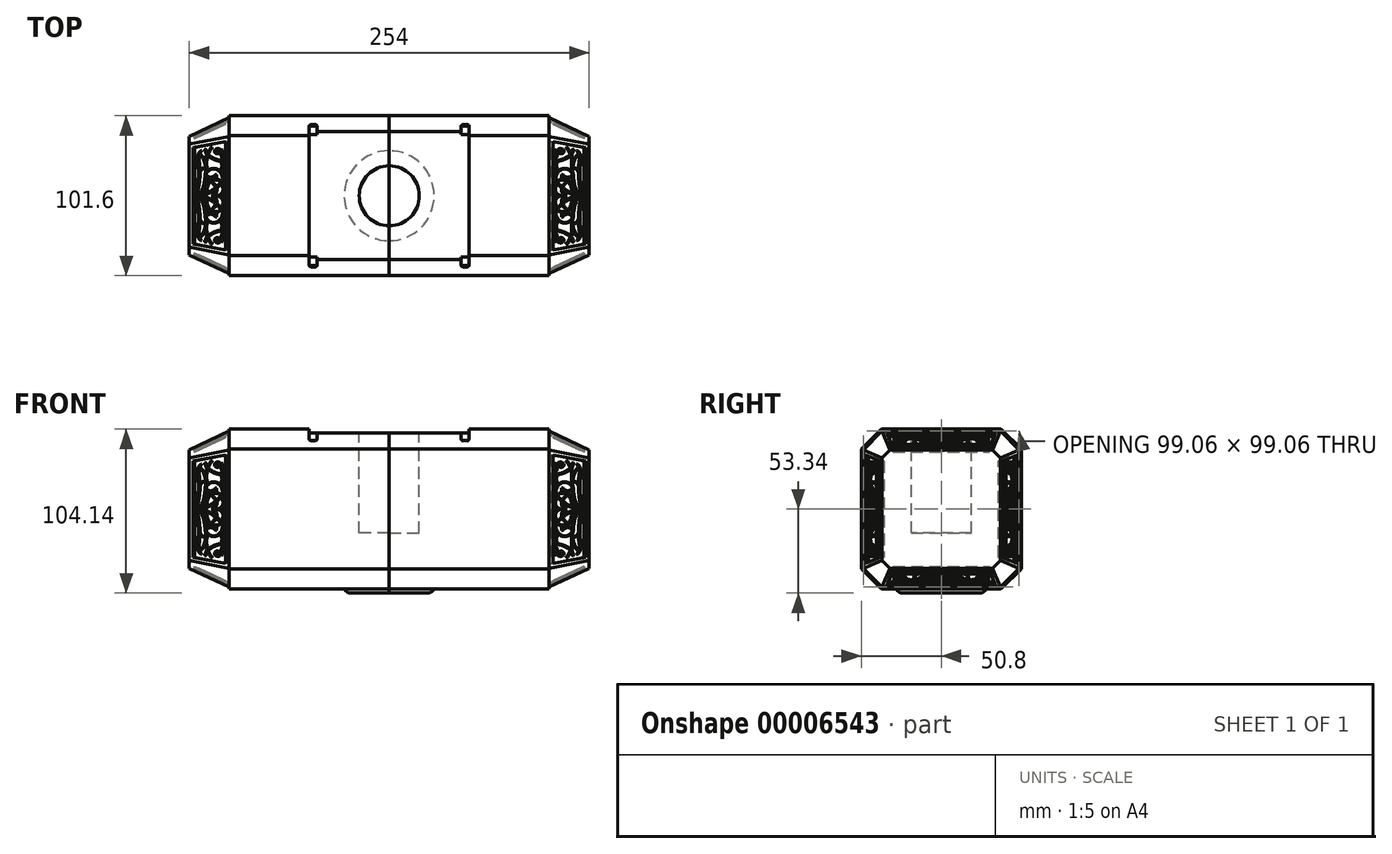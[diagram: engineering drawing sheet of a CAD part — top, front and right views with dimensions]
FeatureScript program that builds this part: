
annotation { "Feature Type Name" : "Feature", "Feature Type Description" : "" }
export const myFeature = defineFeature(function(context is Context, id is Id, definition is map)
    precondition{}
    {
        {
            var Q0;
            Q0=qCreatedBy(makeId("Top.planeOp"),FACE);
            var sketch = newSketch(context, id + "F0", { "sketchPlane" : qUnion([Q0])});
            skLineSegment(sketch, "E0.bottom", {"start": v(-101.6, -50.8) * mm, "end": v(0, -50.8) * mm});
            skLineSegment(sketch, "E0.top", {"start": v(-101.6, 50.8) * mm, "end": v(0, 50.8) * mm});
            skLineSegment(sketch, "E0.left", {"start": v(-101.6, -50.8) * mm, "end": v(-101.6, 50.8) * mm});
            skLineSegment(sketch, "E0.right", {"start": v(0, -50.8) * mm, "end": v(0, 50.8) * mm});
            skSolve(sketch);
        }
        {
            var Q0;
            Q0=makeQuery(id+"F0.imprint","IMPRINT",FACE,{"disambiguationData":[TD([[makeQuery(id+"F0.imprint","IMPRINT",EDGE,{"derivedFrom":sQuery(id+"F0.wireOp",EDGE,"E0.bottom")}),1.0]])]});
            extrude(context, id + "F1", {"entities" : qUnion([Q0]), "depth" : 101.6 * mm});
        }
        {
            var Q0;
            Q0=makeQuery(id+"F1.opExtrude","CAP_EDGE",EDGE,{"disambiguationData":[OSD([sQuery(id+"F0.wireOp",EDGE,"E0.bottom")])],"isStart":false});
            var Q1;
            Q1=makeQuery(id+"F1.opExtrude","CAP_EDGE",EDGE,{"disambiguationData":[OSD([sQuery(id+"F0.wireOp",EDGE,"E0.top")])],"isStart":false});
            var Q2;
            Q2=makeQuery(id+"F1.opExtrude","CAP_EDGE",EDGE,{"disambiguationData":[OSD([sQuery(id+"F0.wireOp",EDGE,"E0.bottom")])],"isStart":true});
            var Q3;
            Q3=makeQuery(id+"F1.opExtrude","CAP_EDGE",EDGE,{"disambiguationData":[OSD([sQuery(id+"F0.wireOp",EDGE,"E0.top")])],"isStart":true});
            chamfer(context, id + "F2", {"entities" : qUnion([Q0, Q1, Q2, Q3]), "width" : 12.7 * mm, "tangentPropagation" : true});
        }
        {
            var Q0;
            Q0=makeQuery(id+"F1.opExtrude","SWEPT_FACE",FACE,{"disambiguationData":[OSD([sQuery(id+"F0.wireOp",EDGE,"E0.left")])]});
            var sketch = newSketch(context, id + "F3", { "sketchPlane" : qUnion([Q0])});
            skLineSegment(sketch, "E1.0", {"start": v(-49.53, 88.37) * mm, "end": v(-37.57, 100.33) * mm});
            skLineSegment(sketch, "E1.1", {"start": v(37.57, 100.33) * mm, "end": v(-37.57, 100.33) * mm});
            skLineSegment(sketch, "E1.2", {"start": v(49.53, 88.37) * mm, "end": v(37.57, 100.33) * mm});
            skLineSegment(sketch, "E1.3", {"start": v(49.53, 88.37) * mm, "end": v(49.53, 13.23) * mm});
            skLineSegment(sketch, "E1.4", {"start": v(49.53, 13.23) * mm, "end": v(37.57, 1.27) * mm});
            skLineSegment(sketch, "E1.5", {"start": v(-49.53, 88.37) * mm, "end": v(-49.53, 13.23) * mm});
            skLineSegment(sketch, "E1.6", {"start": v(37.57, 1.27) * mm, "end": v(-37.57, 1.27) * mm});
            skLineSegment(sketch, "E1.7", {"start": v(-49.53, 13.23) * mm, "end": v(-37.57, 1.27) * mm});
            skSolve(sketch);
        }
        {
            var Q0;
            Q0 = qSketchRegion(id + "F3", true);
            extrude(context, id + "F4", {"entities" : qUnion([Q0]), "operationType" : NewBodyOperationType.ADD, "depth" : 25.4 * mm});
        }
        {
            var Q0;
            Q0=makeQuery(id+"F4.opExtrude","CAP_FACE",FACE,{"disambiguationData":[OSD([sQuery(id+"F3.wireOp",EDGE,"E1.0"),sQuery(id+"F3.wireOp",EDGE,"E1.1"),sQuery(id+"F3.wireOp",EDGE,"E1.2"),sQuery(id+"F3.wireOp",EDGE,"E1.3"),sQuery(id+"F3.wireOp",EDGE,"E1.4"),sQuery(id+"F3.wireOp",EDGE,"E1.5"),sQuery(id+"F3.wireOp",EDGE,"E1.6"),sQuery(id+"F3.wireOp",EDGE,"E1.7")])],"isStart":false});
            chamfer(context, id + "F5", {"entities" : qUnion([Q0]), "chamferType" : ChamferType.OFFSET_ANGLE, "width" : 25.4 * mm, "oppositeDirection" : false, "angle" : 25 * degree, "tangentPropagation" : true});
        }
        {
            var Q0;
            Q0=makeQuery(id+"F5.opChamfer","BLEND_FACE",FACE,{"disambiguationData":[OSD([sQuery(id+"F3.wireOp",EDGE,"E1.1")])]});
            var sketch = newSketch(context, id + "F6", { "sketchPlane" : qUnion([Q0])});
            skLineSegment(sketch, "E2.0", {"start": v(-75.17, -30.53) * mm, "end": v(-52.22, -34.55) * mm});
            skLineSegment(sketch, "E2.1", {"start": v(-75.17, -30.53) * mm, "end": v(-75.17, 30.53) * mm});
            skLineSegment(sketch, "E2.2", {"start": v(-52.22, 34.55) * mm, "end": v(-75.17, 30.53) * mm});
            skLineSegment(sketch, "E2.3", {"start": v(-52.22, -34.55) * mm, "end": v(-52.22, 34.55) * mm});
            skSolve(sketch);
        }
        {
            var Q0;
            Q0=makeQuery(id+"F6.imprint","IMPRINT",FACE,{"disambiguationData":[TD([[makeQuery(id+"F6.imprint","IMPRINT",EDGE,{"derivedFrom":sQuery(id+"F6.wireOp",EDGE,"E2.0")}),1.0]])]});
            extrude(context, id + "F7", {"entities" : qUnion([Q0]), "operationType" : NewBodyOperationType.REMOVE, "oppositeDirection" : true, "depth" : 2.54 * mm});
        }
        {
            var Q0;
            Q0=makeQuery(id+"F7.boolean.opBoolean","COPY",FACE,{"derivedFrom":makeQuery(id+"F7.opExtrude","CAP_FACE",FACE,{"disambiguationData":[OSD([sQuery(id+"F6.wireOp",EDGE,"E2.0"),sQuery(id+"F6.wireOp",EDGE,"E2.1"),sQuery(id+"F6.wireOp",EDGE,"E2.2"),sQuery(id+"F6.wireOp",EDGE,"E2.3")])],"isStart":false})});
            var sketch = newSketch(context, id + "F8", { "sketchPlane" : qUnion([Q0])});
            skLineSegment(sketch, "E3", {"start": v(-52.22, 34.55) * mm, "end": v(-52.22, -34.55) * mm});
            skLineSegment(sketch, "E4", {"start": v(-52.22, -34.55) * mm, "end": v(-75.17, -30.53) * mm, "construction": true});
            skLineSegment(sketch, "E5", {"start": v(-75.17, -30.53) * mm, "end": v(-75.17, 30.53) * mm});
            skLineSegment(sketch, "E6", {"start": v(-75.17, 30.53) * mm, "end": v(-52.22, 34.55) * mm, "construction": true});
            skLineSegment(sketch, "E7", {"start": v(-52.22, 0) * mm, "end": v(-75.17, 0) * mm, "construction": true});
            skArc(sketch, "E8", {"start": v(-55.35, -9.61) * mm, "mid": v(-55.7, -9.17) * mm, "end": v(-56.07, -8.74) * mm});
            skArc(sketch, "E9", {"start": v(-66.68, -14.4) * mm, "mid": v(-59.35, -16.72) * mm, "end": v(-55.08, -10.33) * mm});
            skArc(sketch, "E10", {"start": v(-59.94, -13.49) * mm, "mid": v(-63.02, -11.7) * mm, "end": v(-66.45, -12.68) * mm});
            skLineSegment(sketch, "E11", {"start": v(-59.94, -13.08) * mm, "end": v(-59.94, -10.38) * mm});
            skPoint(sketch, "E12.visualSharp", {"position": v(-55.12, -9.91) * mm});
            skArc(sketch, "E12.filletArc", {"start": v(-55.08, -10.33) * mm, "mid": v(-55.16, -9.95) * mm, "end": v(-55.35, -9.61) * mm});
            skPoint(sketch, "E13.visualSharp", {"position": v(-67.23, -13.49) * mm});
            skArc(sketch, "E13.filletArc", {"start": v(-66.45, -12.68) * mm, "mid": v(-66.9, -13.5) * mm, "end": v(-66.68, -14.4) * mm});
            skArc(sketch, "E14.0", {"start": v(-66.43, -15.12) * mm, "mid": v(-62.16, -17.3) * mm, "end": v(-57.53, -16.05) * mm});
            skArc(sketch, "E14.1", {"start": v(-66.61, -12.48) * mm, "mid": v(-66.77, -12.63) * mm, "end": v(-66.9, -12.8) * mm});
            skArc(sketch, "E14.2", {"start": v(-59.94, -13.08) * mm, "mid": v(-63.15, -11.43) * mm, "end": v(-66.61, -12.48) * mm});
            skLineSegment(sketch, "E15", {"start": v(-59.94, -13.49) * mm, "end": v(-59.6, -13.49) * mm});
            skLineSegment(sketch, "E16", {"start": v(-59.6, -10.38) * mm, "end": v(-59.6, -13.49) * mm});
            skArc(sketch, "E17", {"start": v(-59.6, -10.38) * mm, "mid": v(-57.65, -9.95) * mm, "end": v(-56.07, -8.74) * mm});
            skArc(sketch, "E18", {"start": v(-66.43, -1.56) * mm, "mid": v(-66.13, -6.4) * mm, "end": v(-62.66, -9.81) * mm});
            skArc(sketch, "E19.0", {"start": v(-59.6, -10.08) * mm, "mid": v(-57.78, -9.68) * mm, "end": v(-56.3, -8.54) * mm});
            skLineSegment(sketch, "E19.1", {"start": v(-59.94, -10.08) * mm, "end": v(-59.6, -10.08) * mm});
            skArc(sketch, "E19.2", {"start": v(-66.15, -1.65) * mm, "mid": v(-65.18, -7.43) * mm, "end": v(-59.94, -10.08) * mm});
            skArc(sketch, "E20", {"start": v(-67.23, -13.49) * mm, "mid": v(-68.26, -6.62) * mm, "end": v(-71.17, -0.32) * mm});
            skArc(sketch, "E21.trimOffspring", {"start": v(-66.9, -12.8) * mm, "mid": v(-67.19, -9.87) * mm, "end": v(-67.81, -7) * mm});
            skArc(sketch, "E22", {"start": v(-67.23, -13.49) * mm, "mid": v(-67.12, -14.04) * mm, "end": v(-66.89, -14.55) * mm});
            skArc(sketch, "E23.trimOffspring", {"start": v(-71.17, -0.32) * mm, "mid": v(-72.36, -0.16) * mm, "end": v(-73.55, -0.05) * mm});
            skArc(sketch, "E24.trimOffspring", {"start": v(-66.43, -1.56) * mm, "mid": v(-68.55, -0.88) * mm, "end": v(-70.73, -0.4) * mm});
            skArc(sketch, "E25", {"start": v(-56.3, -8.54) * mm, "mid": v(-57.92, -6.92) * mm, "end": v(-59.67, -5.43) * mm});
            skArc(sketch, "E26", {"start": v(-67.81, -7) * mm, "mid": v(-64.27, -9.61) * mm, "end": v(-59.94, -10.38) * mm});
            skArc(sketch, "E27", {"start": v(-68, -6.35) * mm, "mid": v(-65.6, -8.49) * mm, "end": v(-62.66, -9.81) * mm});
            skArc(sketch, "E28.trimOffspring", {"start": v(-68, -6.35) * mm, "mid": v(-69.17, -3.28) * mm, "end": v(-70.73, -0.4) * mm});
            skArc(sketch, "E29", {"start": v(-55.06, -9.54) * mm, "mid": v(-57.13, -7.05) * mm, "end": v(-59.52, -4.87) * mm});
            skArc(sketch, "E30", {"start": v(-54.83, -10.31) * mm, "mid": v(-54.92, -9.92) * mm, "end": v(-55.06, -9.54) * mm});
            skArc(sketch, "E31", {"start": v(-72.61, -22.4) * mm, "mid": v(-71.93, -11.1) * mm, "end": v(-74.2, -0.02) * mm});
            skArc(sketch, "E32", {"start": v(-72.61, -22.4) * mm, "mid": v(-72.38, -25.91) * mm, "end": v(-70.08, -28.6) * mm});
            skArc(sketch, "E33", {"start": v(-71.93, -22.54) * mm, "mid": v(-71.64, -25.76) * mm, "end": v(-70.08, -28.6) * mm});
            skArc(sketch, "E34", {"start": v(-71.93, -22.54) * mm, "mid": v(-71.5, -18.93) * mm, "end": v(-71.33, -15.3) * mm});
            skArc(sketch, "E35.trimOffspring", {"start": v(-74.2, -0.02) * mm, "mid": v(-74.68, 0) * mm, "end": v(-75.17, 0) * mm});
            skArc(sketch, "E36", {"start": v(-69.62, -24.91) * mm, "mid": v(-67.26, -20) * mm, "end": v(-66.89, -14.55) * mm});
            skArc(sketch, "E37", {"start": v(-69.6, -24.94) * mm, "mid": v(-68.07, -22.87) * mm, "end": v(-67, -20.54) * mm});
            skArc(sketch, "E38", {"start": v(-66.6, -19.05) * mm, "mid": v(-66.52, -22.38) * mm, "end": v(-65.74, -25.62) * mm});
            skArc(sketch, "E39", {"start": v(-67, -20.54) * mm, "mid": v(-66.8, -23.3) * mm, "end": v(-66.02, -25.97) * mm});
            skArc(sketch, "E40", {"start": v(-69.62, -24.91) * mm, "mid": v(-70.07, -25.46) * mm, "end": v(-69.6, -24.94) * mm});
            skArc(sketch, "E41", {"start": v(-63.4, -29.97) * mm, "mid": v(-62.9, -30.5) * mm, "end": v(-63.37, -29.95) * mm});
            skArc(sketch, "E42.trimOffspring", {"start": v(-66.6, -19.05) * mm, "mid": v(-66.36, -17.1) * mm, "end": v(-66.43, -15.12) * mm});
            skArc(sketch, "E43", {"start": v(-71.33, -14.67) * mm, "mid": v(-70.33, -16.2) * mm, "end": v(-68.84, -17.28) * mm});
            skArc(sketch, "E44", {"start": v(-71.33, -15.3) * mm, "mid": v(-70.26, -16.63) * mm, "end": v(-68.84, -17.59) * mm});
            skArc(sketch, "E45", {"start": v(-68.84, -17.59) * mm, "mid": v(-68.43, -17.43) * mm, "end": v(-68.84, -17.28) * mm});
            skArc(sketch, "E46.trimOffspring", {"start": v(-71.33, -14.67) * mm, "mid": v(-71.9, -7.28) * mm, "end": v(-73.55, -0.05) * mm});
            skArc(sketch, "E47", {"start": v(-56.91, -22) * mm, "mid": v(-55.44, -18.83) * mm, "end": v(-57.53, -16.05) * mm});
            skArc(sketch, "E48", {"start": v(-56.63, -22.43) * mm, "mid": v(-55.08, -18.89) * mm, "end": v(-56.8, -15.42) * mm});
            skArc(sketch, "E49", {"start": v(-56.91, -22) * mm, "mid": v(-60.9, -22.98) * mm, "end": v(-64.64, -24.68) * mm});
            skArc(sketch, "E50", {"start": v(-56.63, -22.43) * mm, "mid": v(-60.65, -23.45) * mm, "end": v(-64.33, -25.34) * mm});
            skArc(sketch, "E51", {"start": v(-64.64, -24.68) * mm, "mid": v(-65.22, -25.11) * mm, "end": v(-65.74, -25.62) * mm});
            skArc(sketch, "E52", {"start": v(-64.33, -25.34) * mm, "mid": v(-64.96, -25.72) * mm, "end": v(-65.51, -26.2) * mm});
            skArc(sketch, "E53", {"start": v(-67.08, -28.43) * mm, "mid": v(-67.42, -29.28) * mm, "end": v(-66.7, -28.71) * mm});
            skArc(sketch, "E54.trimOffspring", {"start": v(-65.51, -26.2) * mm, "mid": v(-64.57, -28.15) * mm, "end": v(-63.37, -29.95) * mm});
            skArc(sketch, "E55.trimOffspring", {"start": v(-66.02, -25.97) * mm, "mid": v(-66.7, -27.13) * mm, "end": v(-67.08, -28.43) * mm});
            skArc(sketch, "E56.trimOffspring", {"start": v(-65.78, -26.51) * mm, "mid": v(-64.73, -28.34) * mm, "end": v(-63.4, -29.97) * mm});
            skArc(sketch, "E57.trimOffspring", {"start": v(-65.78, -26.51) * mm, "mid": v(-66.4, -27.55) * mm, "end": v(-66.7, -28.71) * mm});
            skArc(sketch, "E58.trimOffspring", {"start": v(-56.8, -15.42) * mm, "mid": v(-56.04, -14.53) * mm, "end": v(-55.46, -13.53) * mm});
            skArc(sketch, "E59", {"start": v(-55.02, -24.61) * mm, "mid": v(-53.57, -18.63) * mm, "end": v(-55.12, -12.66) * mm});
            skArc(sketch, "E60", {"start": v(-55.02, -24.61) * mm, "mid": v(-55.54, -26.86) * mm, "end": v(-55.02, -29.1) * mm});
            skArc(sketch, "E61", {"start": v(-55.43, -24.24) * mm, "mid": v(-54.08, -18.88) * mm, "end": v(-55.46, -13.53) * mm});
            skArc(sketch, "E62", {"start": v(-55.43, -24.24) * mm, "mid": v(-55.84, -25.25) * mm, "end": v(-55.99, -26.33) * mm});
            skArc(sketch, "E63.trimOffspring", {"start": v(-55.12, -12.66) * mm, "mid": v(-54.87, -11.5) * mm, "end": v(-54.83, -10.31) * mm});
            skArc(sketch, "E64", {"start": v(-61.43, 0) * mm, "mid": v(-61.75, -1) * mm, "end": v(-61.34, -1.96) * mm});
            skArc(sketch, "E65", {"start": v(-61.69, 0) * mm, "mid": v(-62.06, -1.15) * mm, "end": v(-61.47, -2.21) * mm});
            skArc(sketch, "E66", {"start": v(-61.47, -2.21) * mm, "mid": v(-60.8, -2.33) * mm, "end": v(-60.15, -2.07) * mm});
            skArc(sketch, "E67", {"start": v(-61.34, -1.96) * mm, "mid": v(-60.78, -2.05) * mm, "end": v(-60.27, -1.82) * mm});
            skArc(sketch, "E68", {"start": v(-60.55, 0) * mm, "mid": v(-60.67, -0.95) * mm, "end": v(-60.27, -1.82) * mm});
            skArc(sketch, "E69", {"start": v(-60.18, 0) * mm, "mid": v(-60.26, -1.21) * mm, "end": v(-59.75, -2.32) * mm});
            skArc(sketch, "E70", {"start": v(-61.25, -7.6) * mm, "mid": v(-60.3, -6.64) * mm, "end": v(-59.67, -5.43) * mm});
            skArc(sketch, "E71", {"start": v(-61.48, -7.27) * mm, "mid": v(-60.56, -6.36) * mm, "end": v(-59.96, -5.2) * mm});
            skArc(sketch, "E72", {"start": v(-61.48, -7.27) * mm, "mid": v(-61.67, -7.64) * mm, "end": v(-61.25, -7.6) * mm});
            skArc(sketch, "E73.trimOffspring", {"start": v(-59.8, -4.64) * mm, "mid": v(-64.73, -1.7) * mm, "end": v(-70.2, 0) * mm});
            skArc(sketch, "E74.trimOffspring", {"start": v(-59.52, -4.87) * mm, "mid": v(-59.45, -3.57) * mm, "end": v(-59.75, -2.32) * mm});
            skArc(sketch, "E75.trimOffspring", {"start": v(-59.96, -5.2) * mm, "mid": v(-62.94, -3.23) * mm, "end": v(-66.15, -1.65) * mm});
            skArc(sketch, "E76.trimOffspring", {"start": v(-59.8, -4.64) * mm, "mid": v(-59.77, -3.33) * mm, "end": v(-60.15, -2.07) * mm});
            skArc(sketch, "E77", {"start": v(-59.98, -29.41) * mm, "mid": v(-57.3, -29.62) * mm, "end": v(-55.88, -27.35) * mm});
            skArc(sketch, "E78", {"start": v(-59.5, -28.83) * mm, "mid": v(-57.13, -28.43) * mm, "end": v(-55.99, -26.33) * mm});
            skArc(sketch, "E79", {"start": v(-57.78, -27.3) * mm, "mid": v(-59.28, -27.36) * mm, "end": v(-59.5, -28.83) * mm});
            skArc(sketch, "E80", {"start": v(-57.78, -27.3) * mm, "mid": v(-60.12, -27.07) * mm, "end": v(-59.98, -29.41) * mm});
            skArc(sketch, "E81.trimOffspring", {"start": v(-55.88, -27.35) * mm, "mid": v(-55.55, -28.28) * mm, "end": v(-55.02, -29.1) * mm});
            skArc(sketch, "E82", {"start": v(-54.19, -5.3) * mm, "mid": v(-54.2, -2.5) * mm, "end": v(-55.5, 0) * mm});
            skArc(sketch, "E83", {"start": v(-54.19, -5.3) * mm, "mid": v(-54.63, -7.58) * mm, "end": v(-53.98, -9.8) * mm});
            skArc(sketch, "E84", {"start": v(-55.16, -2.34) * mm, "mid": v(-57.14, -0.6) * mm, "end": v(-59.71, 0) * mm});
            skArc(sketch, "E85", {"start": v(-54.93, -5.38) * mm, "mid": v(-54.65, -3.83) * mm, "end": v(-55.16, -2.34) * mm});
            skArc(sketch, "E86", {"start": v(-54.93, -5.38) * mm, "mid": v(-55.04, -7.72) * mm, "end": v(-53.98, -9.8) * mm});
            skArc(sketch, "E87.0.MirrorCS", {"start": v(-55.08, 10.33) * mm, "mid": v(-55.16, 9.95) * mm, "end": v(-55.35, 9.61) * mm});
            skArc(sketch, "E87.1.MirrorCS", {"start": v(-66.61, 12.48) * mm, "mid": v(-66.77, 12.63) * mm, "end": v(-66.9, 12.8) * mm});
            skLineSegment(sketch, "E87.2.MirrorCS", {"start": v(-59.94, 13.49) * mm, "end": v(-59.6, 13.49) * mm});
            skArc(sketch, "E87.3.MirrorCS", {"start": v(-55.35, 9.61) * mm, "mid": v(-55.7, 9.17) * mm, "end": v(-56.07, 8.74) * mm});
            skPoint(sketch, "E87.4.MirrorP", {"position": v(-55.12, 9.91) * mm});
            skArc(sketch, "E87.5.MirrorCS", {"start": v(-68.84, 17.59) * mm, "mid": v(-68.43, 17.43) * mm, "end": v(-68.84, 17.28) * mm});
            skArc(sketch, "E87.6.MirrorCS", {"start": v(-55.43, 24.24) * mm, "mid": v(-54.08, 18.88) * mm, "end": v(-55.46, 13.53) * mm});
            skArc(sketch, "E87.7.MirrorCS", {"start": v(-55.06, 9.54) * mm, "mid": v(-57.13, 7.05) * mm, "end": v(-59.52, 4.87) * mm});
            skArc(sketch, "E87.8.MirrorCS", {"start": v(-59.98, 29.41) * mm, "mid": v(-57.3, 29.62) * mm, "end": v(-55.88, 27.35) * mm});
            skArc(sketch, "E87.9.MirrorCS", {"start": v(-60.18, 0) * mm, "mid": v(-60.26, 1.21) * mm, "end": v(-59.75, 2.32) * mm});
            skArc(sketch, "E87.10.MirrorCS", {"start": v(-67.08, 28.43) * mm, "mid": v(-67.42, 29.28) * mm, "end": v(-66.7, 28.71) * mm});
            skArc(sketch, "E87.11.MirrorCS", {"start": v(-69.6, 24.94) * mm, "mid": v(-68.07, 22.87) * mm, "end": v(-67, 20.54) * mm});
            skArc(sketch, "E87.12.MirrorCS", {"start": v(-66.9, 12.8) * mm, "mid": v(-67.19, 9.87) * mm, "end": v(-67.81, 7) * mm});
            skArc(sketch, "E87.13.MirrorCS", {"start": v(-54.93, 5.38) * mm, "mid": v(-54.65, 3.83) * mm, "end": v(-55.16, 2.34) * mm});
            skArc(sketch, "E87.14.MirrorCS", {"start": v(-68, 6.35) * mm, "mid": v(-65.6, 8.49) * mm, "end": v(-62.66, 9.81) * mm});
            skArc(sketch, "E87.15.MirrorCS", {"start": v(-71.33, 14.67) * mm, "mid": v(-70.33, 16.2) * mm, "end": v(-68.84, 17.28) * mm});
            skArc(sketch, "E87.16.MirrorCS", {"start": v(-55.02, 24.61) * mm, "mid": v(-53.57, 18.63) * mm, "end": v(-55.12, 12.66) * mm});
            skArc(sketch, "E87.17.MirrorCS", {"start": v(-59.96, 5.2) * mm, "mid": v(-62.94, 3.23) * mm, "end": v(-66.15, 1.65) * mm});
            skArc(sketch, "E87.18.MirrorCS", {"start": v(-55.43, 24.24) * mm, "mid": v(-55.84, 25.25) * mm, "end": v(-55.99, 26.33) * mm});
            skArc(sketch, "E87.19.MirrorCS", {"start": v(-71.33, 14.67) * mm, "mid": v(-71.9, 7.28) * mm, "end": v(-73.55, 0.05) * mm});
            skArc(sketch, "E87.20.MirrorCS", {"start": v(-54.83, 10.31) * mm, "mid": v(-54.92, 9.92) * mm, "end": v(-55.06, 9.54) * mm});
            skArc(sketch, "E87.21.MirrorCS", {"start": v(-59.5, 28.83) * mm, "mid": v(-57.13, 28.43) * mm, "end": v(-55.99, 26.33) * mm});
            skArc(sketch, "E87.22.MirrorCS", {"start": v(-55.16, 2.34) * mm, "mid": v(-57.14, 0.6) * mm, "end": v(-59.71, 0) * mm});
            skArc(sketch, "E87.23.MirrorCS", {"start": v(-64.33, 25.34) * mm, "mid": v(-64.96, 25.72) * mm, "end": v(-65.51, 26.2) * mm});
            skArc(sketch, "E87.24.MirrorCS", {"start": v(-60.55, 0) * mm, "mid": v(-60.67, 0.95) * mm, "end": v(-60.27, 1.82) * mm});
            skArc(sketch, "E87.25.MirrorCS", {"start": v(-67.23, 13.49) * mm, "mid": v(-68.26, 6.62) * mm, "end": v(-71.17, 0.32) * mm});
            skArc(sketch, "E87.26.MirrorCS", {"start": v(-69.62, 24.91) * mm, "mid": v(-67.26, 20) * mm, "end": v(-66.89, 14.55) * mm});
            skArc(sketch, "E87.27.MirrorCS", {"start": v(-67.23, 13.49) * mm, "mid": v(-67.12, 14.04) * mm, "end": v(-66.89, 14.55) * mm});
            skArc(sketch, "E87.28.MirrorCS", {"start": v(-66.6, 19.05) * mm, "mid": v(-66.52, 22.38) * mm, "end": v(-65.74, 25.62) * mm});
            skArc(sketch, "E87.29.MirrorCS", {"start": v(-65.51, 26.2) * mm, "mid": v(-64.57, 28.15) * mm, "end": v(-63.37, 29.95) * mm});
            skArc(sketch, "E87.30.MirrorCS", {"start": v(-66.45, 12.68) * mm, "mid": v(-66.9, 13.5) * mm, "end": v(-66.68, 14.4) * mm});
            skArc(sketch, "E87.31.MirrorCS", {"start": v(-54.19, 5.3) * mm, "mid": v(-54.2, 2.5) * mm, "end": v(-55.5, 0) * mm});
            skArc(sketch, "E87.32.MirrorCS", {"start": v(-61.25, 7.6) * mm, "mid": v(-60.3, 6.64) * mm, "end": v(-59.67, 5.43) * mm});
            skArc(sketch, "E87.33.MirrorCS", {"start": v(-54.93, 5.38) * mm, "mid": v(-55.04, 7.72) * mm, "end": v(-53.98, 9.8) * mm});
            skArc(sketch, "E87.34.MirrorCS", {"start": v(-66.43, 15.12) * mm, "mid": v(-62.16, 17.3) * mm, "end": v(-57.53, 16.05) * mm});
            skArc(sketch, "E87.35.MirrorCS", {"start": v(-61.47, 2.21) * mm, "mid": v(-60.8, 2.33) * mm, "end": v(-60.15, 2.07) * mm});
            skArc(sketch, "E87.36.MirrorCS", {"start": v(-56.63, 22.43) * mm, "mid": v(-60.65, 23.45) * mm, "end": v(-64.33, 25.34) * mm});
            skArc(sketch, "E87.37.MirrorCS", {"start": v(-71.93, 22.54) * mm, "mid": v(-71.5, 18.93) * mm, "end": v(-71.33, 15.3) * mm});
            skArc(sketch, "E87.38.MirrorCS", {"start": v(-55.12, 12.66) * mm, "mid": v(-54.87, 11.5) * mm, "end": v(-54.83, 10.31) * mm});
            skLineSegment(sketch, "E87.39.MirrorCS", {"start": v(-59.94, 10.08) * mm, "end": v(-59.6, 10.08) * mm});
            skArc(sketch, "E87.40.MirrorCS", {"start": v(-56.91, 22) * mm, "mid": v(-55.44, 18.83) * mm, "end": v(-57.53, 16.05) * mm});
            skArc(sketch, "E87.41.MirrorCS", {"start": v(-59.6, 10.38) * mm, "mid": v(-57.65, 9.95) * mm, "end": v(-56.07, 8.74) * mm});
            skArc(sketch, "E87.42.MirrorCS", {"start": v(-72.61, 22.4) * mm, "mid": v(-71.93, 11.1) * mm, "end": v(-74.2, 0.02) * mm});
            skArc(sketch, "E87.43.MirrorCS", {"start": v(-57.78, 27.3) * mm, "mid": v(-59.28, 27.36) * mm, "end": v(-59.5, 28.83) * mm});
            skLineSegment(sketch, "E87.44.MirrorCS", {"start": v(-59.6, 10.38) * mm, "end": v(-59.6, 13.49) * mm});
            skArc(sketch, "E87.45.MirrorCS", {"start": v(-56.3, 8.54) * mm, "mid": v(-57.92, 6.92) * mm, "end": v(-59.67, 5.43) * mm});
            skArc(sketch, "E87.46.MirrorCS", {"start": v(-59.8, 4.64) * mm, "mid": v(-64.73, 1.7) * mm, "end": v(-70.2, 0) * mm});
            skArc(sketch, "E87.47.MirrorCS", {"start": v(-63.4, 29.97) * mm, "mid": v(-62.9, 30.5) * mm, "end": v(-63.37, 29.95) * mm});
            skArc(sketch, "E87.48.MirrorCS", {"start": v(-65.78, 26.51) * mm, "mid": v(-66.4, 27.55) * mm, "end": v(-66.7, 28.71) * mm});
            skArc(sketch, "E87.49.MirrorCS", {"start": v(-59.94, 13.08) * mm, "mid": v(-63.15, 11.43) * mm, "end": v(-66.61, 12.48) * mm});
            skArc(sketch, "E87.50.MirrorCS", {"start": v(-66.43, 1.56) * mm, "mid": v(-68.55, 0.88) * mm, "end": v(-70.73, 0.4) * mm});
            skArc(sketch, "E87.51.MirrorCS", {"start": v(-66.68, 14.4) * mm, "mid": v(-59.35, 16.72) * mm, "end": v(-55.08, 10.33) * mm});
            skPoint(sketch, "E87.52.MirrorP", {"position": v(-67.23, 13.49) * mm});
            skArc(sketch, "E87.53.MirrorCS", {"start": v(-59.94, 13.49) * mm, "mid": v(-63.02, 11.7) * mm, "end": v(-66.45, 12.68) * mm});
            skLineSegment(sketch, "E87.54.MirrorCS", {"start": v(-59.94, 13.08) * mm, "end": v(-59.94, 10.38) * mm});
            skArc(sketch, "E87.55.MirrorCS", {"start": v(-69.62, 24.91) * mm, "mid": v(-70.07, 25.46) * mm, "end": v(-69.6, 24.94) * mm});
            skArc(sketch, "E87.56.MirrorCS", {"start": v(-71.33, 15.3) * mm, "mid": v(-70.26, 16.63) * mm, "end": v(-68.84, 17.59) * mm});
            skArc(sketch, "E87.57.MirrorCS", {"start": v(-68, 6.35) * mm, "mid": v(-69.17, 3.28) * mm, "end": v(-70.73, 0.4) * mm});
            skArc(sketch, "E87.58.MirrorCS", {"start": v(-59.8, 4.64) * mm, "mid": v(-59.77, 3.33) * mm, "end": v(-60.15, 2.07) * mm});
            skArc(sketch, "E87.59.MirrorCS", {"start": v(-61.69, 0) * mm, "mid": v(-62.06, 1.15) * mm, "end": v(-61.47, 2.21) * mm});
            skArc(sketch, "E87.60.MirrorCS", {"start": v(-56.91, 22) * mm, "mid": v(-60.9, 22.98) * mm, "end": v(-64.64, 24.68) * mm});
            skArc(sketch, "E87.61.MirrorCS", {"start": v(-59.6, 10.08) * mm, "mid": v(-57.78, 9.68) * mm, "end": v(-56.3, 8.54) * mm});
            skArc(sketch, "E87.62.MirrorCS", {"start": v(-55.02, 24.61) * mm, "mid": v(-55.54, 26.86) * mm, "end": v(-55.02, 29.1) * mm});
            skArc(sketch, "E87.63.MirrorCS", {"start": v(-71.93, 22.54) * mm, "mid": v(-71.64, 25.76) * mm, "end": v(-70.08, 28.6) * mm});
            skArc(sketch, "E87.64.MirrorCS", {"start": v(-54.19, 5.3) * mm, "mid": v(-54.63, 7.58) * mm, "end": v(-53.98, 9.8) * mm});
            skArc(sketch, "E87.65.MirrorCS", {"start": v(-61.34, 1.96) * mm, "mid": v(-60.78, 2.05) * mm, "end": v(-60.27, 1.82) * mm});
            skArc(sketch, "E87.66.MirrorCS", {"start": v(-74.2, 0.02) * mm, "mid": v(-74.68, 0) * mm, "end": v(-75.17, 0) * mm});
            skArc(sketch, "E87.67.MirrorCS", {"start": v(-66.15, 1.65) * mm, "mid": v(-65.18, 7.43) * mm, "end": v(-59.94, 10.08) * mm});
            skArc(sketch, "E87.68.MirrorCS", {"start": v(-67, 20.54) * mm, "mid": v(-66.8, 23.3) * mm, "end": v(-66.02, 25.97) * mm});
            skArc(sketch, "E87.69.MirrorCS", {"start": v(-56.63, 22.43) * mm, "mid": v(-55.08, 18.89) * mm, "end": v(-56.8, 15.42) * mm});
            skArc(sketch, "E87.70.MirrorCS", {"start": v(-71.17, 0.32) * mm, "mid": v(-72.36, 0.16) * mm, "end": v(-73.55, 0.05) * mm});
            skArc(sketch, "E87.71.MirrorCS", {"start": v(-55.88, 27.35) * mm, "mid": v(-55.55, 28.28) * mm, "end": v(-55.02, 29.1) * mm});
            skArc(sketch, "E87.72.MirrorCS", {"start": v(-61.43, 0) * mm, "mid": v(-61.75, 1) * mm, "end": v(-61.34, 1.96) * mm});
            skArc(sketch, "E87.73.MirrorCS", {"start": v(-59.52, 4.87) * mm, "mid": v(-59.45, 3.57) * mm, "end": v(-59.75, 2.32) * mm});
            skArc(sketch, "E87.74.MirrorCS", {"start": v(-64.64, 24.68) * mm, "mid": v(-65.22, 25.11) * mm, "end": v(-65.74, 25.62) * mm});
            skArc(sketch, "E87.75.MirrorCS", {"start": v(-66.02, 25.97) * mm, "mid": v(-66.7, 27.13) * mm, "end": v(-67.08, 28.43) * mm});
            skArc(sketch, "E87.76.MirrorCS", {"start": v(-61.48, 7.27) * mm, "mid": v(-60.56, 6.36) * mm, "end": v(-59.96, 5.2) * mm});
            skArc(sketch, "E87.77.MirrorCS", {"start": v(-67.81, 7) * mm, "mid": v(-64.27, 9.61) * mm, "end": v(-59.94, 10.38) * mm});
            skArc(sketch, "E87.78.MirrorCS", {"start": v(-66.6, 19.05) * mm, "mid": v(-66.36, 17.1) * mm, "end": v(-66.43, 15.12) * mm});
            skArc(sketch, "E87.79.MirrorCS", {"start": v(-57.78, 27.3) * mm, "mid": v(-60.12, 27.07) * mm, "end": v(-59.98, 29.41) * mm});
            skArc(sketch, "E87.80.MirrorCS", {"start": v(-61.48, 7.27) * mm, "mid": v(-61.67, 7.64) * mm, "end": v(-61.25, 7.6) * mm});
            skArc(sketch, "E87.81.MirrorCS", {"start": v(-72.61, 22.4) * mm, "mid": v(-72.38, 25.91) * mm, "end": v(-70.08, 28.6) * mm});
            skArc(sketch, "E87.82.MirrorCS", {"start": v(-65.78, 26.51) * mm, "mid": v(-64.73, 28.34) * mm, "end": v(-63.4, 29.97) * mm});
            skArc(sketch, "E87.83.MirrorCS", {"start": v(-56.8, 15.42) * mm, "mid": v(-56.04, 14.53) * mm, "end": v(-55.46, 13.53) * mm});
            skArc(sketch, "E87.84.MirrorCS", {"start": v(-66.43, 1.56) * mm, "mid": v(-66.13, 6.4) * mm, "end": v(-62.66, 9.81) * mm});
            skSolve(sketch);
        }
        {
            var Q0;
            Q0=makeQuery(id+"F8.imprint","IMPRINT",FACE,{"disambiguationData":[TD([[makeQuery(id+"F8.imprint","IMPRINT",EDGE,{"derivedFrom":sQuery(id+"F8.wireOp",EDGE,"E8")}),-1.0]])]});
            var Q1;
            Q1=makeQuery(id+"F8.imprint","IMPRINT",FACE,{"disambiguationData":[TD([[makeQuery(id+"F8.imprint","IMPRINT",EDGE,{"derivedFrom":sQuery(id+"F8.wireOp",EDGE,"E82")}),1.0]])]});
            extrude(context, id + "F9", {"entities" : qUnion([Q0, Q1]), "depth" : 1.27 * mm});
        }
        {
            var Q0;
            Q0=qCreatedBy(makeId("Front.planeOp"),FACE);
            var sketch = newSketch(context, id + "F10", { "sketchPlane" : qUnion([Q0])});
            skLineSegment(sketch, "E88", {"start": v(0, 50.8) * mm, "end": v(68.96, 50.8) * mm});
            skSolve(sketch);
        }
        {
            var Q0;
            Q0=makeQuery(id+"F5.opChamfer","BLEND_FACE",FACE,{"disambiguationData":[OSD([sQuery(id+"F3.wireOp",EDGE,"E1.5")])]});
            var sketch = newSketch(context, id + "F11", { "sketchPlane" : qUnion([Q0])});
            skLineSegment(sketch, "E89.0", {"start": v(96.63, 81.33) * mm, "end": v(73.69, 85.35) * mm});
            skLineSegment(sketch, "E89.1", {"start": v(96.63, 20.27) * mm, "end": v(96.63, 81.33) * mm});
            skLineSegment(sketch, "E89.2", {"start": v(96.63, 20.27) * mm, "end": v(73.69, 16.25) * mm});
            skLineSegment(sketch, "E89.3", {"start": v(73.69, 85.35) * mm, "end": v(73.69, 16.25) * mm});
            skSolve(sketch);
        }
        {
            var Q0;
            Q0=makeQuery(id+"F11.imprint","IMPRINT",FACE,{"disambiguationData":[TD([[makeQuery(id+"F11.imprint","IMPRINT",EDGE,{"derivedFrom":sQuery(id+"F11.wireOp",EDGE,"E89.0")}),1.0]])]});
            extrude(context, id + "F12", {"entities" : qUnion([Q0]), "operationType" : NewBodyOperationType.REMOVE, "oppositeDirection" : true, "depth" : 2.54 * mm});
        }
        {
            var Q0;
            Q0=makeQuery(id+"F5.opChamfer","BLEND_FACE",FACE,{"disambiguationData":[OSD([sQuery(id+"F3.wireOp",EDGE,"E1.6")])]});
            var sketch = newSketch(context, id + "F13", { "sketchPlane" : qUnion([Q0])});
            skLineSegment(sketch, "E90.0", {"start": v(-95.16, 34.55) * mm, "end": v(-118.1, 30.53) * mm});
            skLineSegment(sketch, "E90.1", {"start": v(-95.16, -34.55) * mm, "end": v(-95.16, 34.55) * mm});
            skLineSegment(sketch, "E90.2", {"start": v(-118.1, -30.53) * mm, "end": v(-95.16, -34.55) * mm});
            skLineSegment(sketch, "E90.3", {"start": v(-118.1, 30.53) * mm, "end": v(-118.1, -30.53) * mm});
            skSolve(sketch);
        }
        {
            var Q0;
            Q0=makeQuery(id+"F13.imprint","IMPRINT",FACE,{"disambiguationData":[TD([[makeQuery(id+"F13.imprint","IMPRINT",EDGE,{"derivedFrom":sQuery(id+"F13.wireOp",EDGE,"E90.0")}),1.0]])]});
            extrude(context, id + "F14", {"entities" : qUnion([Q0]), "operationType" : NewBodyOperationType.REMOVE, "oppositeDirection" : true, "depth" : 2.54 * mm});
        }
        {
            var Q0;
            Q0=makeQuery(id+"F5.opChamfer","BLEND_FACE",FACE,{"disambiguationData":[OSD([sQuery(id+"F3.wireOp",EDGE,"E1.3")])]});
            var sketch = newSketch(context, id + "F15", { "sketchPlane" : qUnion([Q0])});
            skLineSegment(sketch, "E91.0", {"start": v(-73.69, 85.35) * mm, "end": v(-96.63, 81.33) * mm});
            skLineSegment(sketch, "E91.1", {"start": v(-73.69, 16.25) * mm, "end": v(-73.69, 85.35) * mm});
            skLineSegment(sketch, "E91.2", {"start": v(-73.69, 16.25) * mm, "end": v(-96.63, 20.27) * mm});
            skLineSegment(sketch, "E91.3", {"start": v(-96.63, 81.33) * mm, "end": v(-96.63, 20.27) * mm});
            skSolve(sketch);
        }
        {
            var Q0;
            Q0=makeQuery(id+"F15.imprint","IMPRINT",FACE,{"disambiguationData":[TD([[makeQuery(id+"F15.imprint","IMPRINT",EDGE,{"derivedFrom":sQuery(id+"F15.wireOp",EDGE,"E91.0")}),1.0]])]});
            extrude(context, id + "F16", {"entities" : qUnion([Q0]), "operationType" : NewBodyOperationType.REMOVE, "oppositeDirection" : true, "depth" : 2.54 * mm});
        }
        {
            var Q0;
            Q0=makeQuery(id+"F9.opExtrude","SWEPT_BODY",BODY,{"disambiguationData":[OSD([sQuery(id+"F8.wireOp",EDGE,"E8"),sQuery(id+"F8.wireOp",EDGE,"E9"),sQuery(id+"F8.wireOp",EDGE,"E10"),sQuery(id+"F8.wireOp",EDGE,"E11"),sQuery(id+"F8.wireOp",EDGE,"E12.filletArc"),sQuery(id+"F8.wireOp",EDGE,"E13.filletArc"),sQuery(id+"F8.wireOp",EDGE,"E14.0"),sQuery(id+"F8.wireOp",EDGE,"E14.1"),sQuery(id+"F8.wireOp",EDGE,"E14.2"),sQuery(id+"F8.wireOp",EDGE,"E15"),sQuery(id+"F8.wireOp",EDGE,"E16"),sQuery(id+"F8.wireOp",EDGE,"E17"),sQuery(id+"F8.wireOp",EDGE,"E18"),sQuery(id+"F8.wireOp",EDGE,"E19.0"),sQuery(id+"F8.wireOp",EDGE,"E19.1"),sQuery(id+"F8.wireOp",EDGE,"E19.2"),sQuery(id+"F8.wireOp",EDGE,"E20"),sQuery(id+"F8.wireOp",EDGE,"E21.trimOffspring"),sQuery(id+"F8.wireOp",EDGE,"E22"),sQuery(id+"F8.wireOp",EDGE,"E23.trimOffspring"),sQuery(id+"F8.wireOp",EDGE,"E24.trimOffspring"),sQuery(id+"F8.wireOp",EDGE,"E25"),sQuery(id+"F8.wireOp",EDGE,"E26"),sQuery(id+"F8.wireOp",EDGE,"E27"),sQuery(id+"F8.wireOp",EDGE,"E28.trimOffspring"),sQuery(id+"F8.wireOp",EDGE,"E29"),sQuery(id+"F8.wireOp",EDGE,"E30"),sQuery(id+"F8.wireOp",EDGE,"E31"),sQuery(id+"F8.wireOp",EDGE,"E32"),sQuery(id+"F8.wireOp",EDGE,"E33"),sQuery(id+"F8.wireOp",EDGE,"E34"),sQuery(id+"F8.wireOp",EDGE,"E35.trimOffspring"),sQuery(id+"F8.wireOp",EDGE,"E36"),sQuery(id+"F8.wireOp",EDGE,"E37"),sQuery(id+"F8.wireOp",EDGE,"E38"),sQuery(id+"F8.wireOp",EDGE,"E39"),sQuery(id+"F8.wireOp",EDGE,"E40"),sQuery(id+"F8.wireOp",EDGE,"E41"),sQuery(id+"F8.wireOp",EDGE,"E42.trimOffspring"),sQuery(id+"F8.wireOp",EDGE,"E43"),sQuery(id+"F8.wireOp",EDGE,"E44"),sQuery(id+"F8.wireOp",EDGE,"E45"),sQuery(id+"F8.wireOp",EDGE,"E46.trimOffspring"),sQuery(id+"F8.wireOp",EDGE,"E47"),sQuery(id+"F8.wireOp",EDGE,"E48"),sQuery(id+"F8.wireOp",EDGE,"E49"),sQuery(id+"F8.wireOp",EDGE,"E50"),sQuery(id+"F8.wireOp",EDGE,"E51"),sQuery(id+"F8.wireOp",EDGE,"E52"),sQuery(id+"F8.wireOp",EDGE,"E53"),sQuery(id+"F8.wireOp",EDGE,"E54.trimOffspring"),sQuery(id+"F8.wireOp",EDGE,"E55.trimOffspring"),sQuery(id+"F8.wireOp",EDGE,"E56.trimOffspring"),sQuery(id+"F8.wireOp",EDGE,"E57.trimOffspring"),sQuery(id+"F8.wireOp",EDGE,"E58.trimOffspring"),sQuery(id+"F8.wireOp",EDGE,"E59"),sQuery(id+"F8.wireOp",EDGE,"E60"),sQuery(id+"F8.wireOp",EDGE,"E61"),sQuery(id+"F8.wireOp",EDGE,"E62"),sQuery(id+"F8.wireOp",EDGE,"E63.trimOffspring"),sQuery(id+"F8.wireOp",EDGE,"E64"),sQuery(id+"F8.wireOp",EDGE,"E65"),sQuery(id+"F8.wireOp",EDGE,"E66"),sQuery(id+"F8.wireOp",EDGE,"E67"),sQuery(id+"F8.wireOp",EDGE,"E68"),sQuery(id+"F8.wireOp",EDGE,"E69"),sQuery(id+"F8.wireOp",EDGE,"E70"),sQuery(id+"F8.wireOp",EDGE,"E71"),sQuery(id+"F8.wireOp",EDGE,"E72"),sQuery(id+"F8.wireOp",EDGE,"E73.trimOffspring"),sQuery(id+"F8.wireOp",EDGE,"E74.trimOffspring"),sQuery(id+"F8.wireOp",EDGE,"E75.trimOffspring"),sQuery(id+"F8.wireOp",EDGE,"E76.trimOffspring"),sQuery(id+"F8.wireOp",EDGE,"E77"),sQuery(id+"F8.wireOp",EDGE,"E78"),sQuery(id+"F8.wireOp",EDGE,"E79"),sQuery(id+"F8.wireOp",EDGE,"E80"),sQuery(id+"F8.wireOp",EDGE,"E81.trimOffspring"),sQuery(id+"F8.wireOp",EDGE,"E87.0.MirrorCS"),sQuery(id+"F8.wireOp",EDGE,"E87.1.MirrorCS"),sQuery(id+"F8.wireOp",EDGE,"E87.2.MirrorCS"),sQuery(id+"F8.wireOp",EDGE,"E87.3.MirrorCS"),sQuery(id+"F8.wireOp",EDGE,"E87.5.MirrorCS"),sQuery(id+"F8.wireOp",EDGE,"E87.6.MirrorCS"),sQuery(id+"F8.wireOp",EDGE,"E87.7.MirrorCS"),sQuery(id+"F8.wireOp",EDGE,"E87.8.MirrorCS"),sQuery(id+"F8.wireOp",EDGE,"E87.9.MirrorCS"),sQuery(id+"F8.wireOp",EDGE,"E87.10.MirrorCS"),sQuery(id+"F8.wireOp",EDGE,"E87.11.MirrorCS"),sQuery(id+"F8.wireOp",EDGE,"E87.12.MirrorCS"),sQuery(id+"F8.wireOp",EDGE,"E87.14.MirrorCS"),sQuery(id+"F8.wireOp",EDGE,"E87.15.MirrorCS"),sQuery(id+"F8.wireOp",EDGE,"E87.16.MirrorCS"),sQuery(id+"F8.wireOp",EDGE,"E87.17.MirrorCS"),sQuery(id+"F8.wireOp",EDGE,"E87.18.MirrorCS"),sQuery(id+"F8.wireOp",EDGE,"E87.19.MirrorCS"),sQuery(id+"F8.wireOp",EDGE,"E87.20.MirrorCS"),sQuery(id+"F8.wireOp",EDGE,"E87.21.MirrorCS"),sQuery(id+"F8.wireOp",EDGE,"E87.23.MirrorCS"),sQuery(id+"F8.wireOp",EDGE,"E87.24.MirrorCS"),sQuery(id+"F8.wireOp",EDGE,"E87.25.MirrorCS"),sQuery(id+"F8.wireOp",EDGE,"E87.26.MirrorCS"),sQuery(id+"F8.wireOp",EDGE,"E87.27.MirrorCS"),sQuery(id+"F8.wireOp",EDGE,"E87.28.MirrorCS"),sQuery(id+"F8.wireOp",EDGE,"E87.29.MirrorCS"),sQuery(id+"F8.wireOp",EDGE,"E87.30.MirrorCS"),sQuery(id+"F8.wireOp",EDGE,"E87.32.MirrorCS"),sQuery(id+"F8.wireOp",EDGE,"E87.34.MirrorCS"),sQuery(id+"F8.wireOp",EDGE,"E87.35.MirrorCS"),sQuery(id+"F8.wireOp",EDGE,"E87.36.MirrorCS"),sQuery(id+"F8.wireOp",EDGE,"E87.37.MirrorCS"),sQuery(id+"F8.wireOp",EDGE,"E87.38.MirrorCS"),sQuery(id+"F8.wireOp",EDGE,"E87.39.MirrorCS"),sQuery(id+"F8.wireOp",EDGE,"E87.40.MirrorCS"),sQuery(id+"F8.wireOp",EDGE,"E87.41.MirrorCS"),sQuery(id+"F8.wireOp",EDGE,"E87.42.MirrorCS"),sQuery(id+"F8.wireOp",EDGE,"E87.43.MirrorCS"),sQuery(id+"F8.wireOp",EDGE,"E87.44.MirrorCS"),sQuery(id+"F8.wireOp",EDGE,"E87.45.MirrorCS"),sQuery(id+"F8.wireOp",EDGE,"E87.46.MirrorCS"),sQuery(id+"F8.wireOp",EDGE,"E87.47.MirrorCS"),sQuery(id+"F8.wireOp",EDGE,"E87.48.MirrorCS"),sQuery(id+"F8.wireOp",EDGE,"E87.49.MirrorCS"),sQuery(id+"F8.wireOp",EDGE,"E87.50.MirrorCS"),sQuery(id+"F8.wireOp",EDGE,"E87.51.MirrorCS"),sQuery(id+"F8.wireOp",EDGE,"E87.53.MirrorCS"),sQuery(id+"F8.wireOp",EDGE,"E87.54.MirrorCS"),sQuery(id+"F8.wireOp",EDGE,"E87.55.MirrorCS"),sQuery(id+"F8.wireOp",EDGE,"E87.56.MirrorCS"),sQuery(id+"F8.wireOp",EDGE,"E87.57.MirrorCS"),sQuery(id+"F8.wireOp",EDGE,"E87.58.MirrorCS"),sQuery(id+"F8.wireOp",EDGE,"E87.59.MirrorCS"),sQuery(id+"F8.wireOp",EDGE,"E87.60.MirrorCS"),sQuery(id+"F8.wireOp",EDGE,"E87.61.MirrorCS"),sQuery(id+"F8.wireOp",EDGE,"E87.62.MirrorCS"),sQuery(id+"F8.wireOp",EDGE,"E87.63.MirrorCS"),sQuery(id+"F8.wireOp",EDGE,"E87.65.MirrorCS"),sQuery(id+"F8.wireOp",EDGE,"E87.66.MirrorCS"),sQuery(id+"F8.wireOp",EDGE,"E87.67.MirrorCS"),sQuery(id+"F8.wireOp",EDGE,"E87.68.MirrorCS"),sQuery(id+"F8.wireOp",EDGE,"E87.69.MirrorCS"),sQuery(id+"F8.wireOp",EDGE,"E87.70.MirrorCS"),sQuery(id+"F8.wireOp",EDGE,"E87.71.MirrorCS"),sQuery(id+"F8.wireOp",EDGE,"E87.72.MirrorCS"),sQuery(id+"F8.wireOp",EDGE,"E87.73.MirrorCS"),sQuery(id+"F8.wireOp",EDGE,"E87.74.MirrorCS"),sQuery(id+"F8.wireOp",EDGE,"E87.75.MirrorCS"),sQuery(id+"F8.wireOp",EDGE,"E87.76.MirrorCS"),sQuery(id+"F8.wireOp",EDGE,"E87.77.MirrorCS"),sQuery(id+"F8.wireOp",EDGE,"E87.78.MirrorCS"),sQuery(id+"F8.wireOp",EDGE,"E87.79.MirrorCS"),sQuery(id+"F8.wireOp",EDGE,"E87.80.MirrorCS"),sQuery(id+"F8.wireOp",EDGE,"E87.81.MirrorCS"),sQuery(id+"F8.wireOp",EDGE,"E87.82.MirrorCS"),sQuery(id+"F8.wireOp",EDGE,"E87.83.MirrorCS"),sQuery(id+"F8.wireOp",EDGE,"E87.84.MirrorCS")])]});
            var Q1;
            Q1=makeQuery(id+"F9.opExtrude","SWEPT_BODY",BODY,{"disambiguationData":[OSD([sQuery(id+"F8.wireOp",EDGE,"E82"),sQuery(id+"F8.wireOp",EDGE,"E83"),sQuery(id+"F8.wireOp",EDGE,"E84"),sQuery(id+"F8.wireOp",EDGE,"E85"),sQuery(id+"F8.wireOp",EDGE,"E86"),sQuery(id+"F8.wireOp",EDGE,"E87.13.MirrorCS"),sQuery(id+"F8.wireOp",EDGE,"E87.31.MirrorCS"),sQuery(id+"F8.wireOp",EDGE,"E87.33.MirrorCS"),sQuery(id+"F8.wireOp",EDGE,"E87.64.MirrorCS"),sQuery(id+"F8.wireOp",EDGE,"E87.22.MirrorCS")])]});
            var Q2;
            Q2=sQuery(id+"F10.wireOp",EDGE,"E88");
            circularPattern(context, id + "F17", {"entities" : qUnion([Q0, Q1]), "axis" : qUnion([Q2]), "angle" : 90 * degree, "instanceCount" : 4});
        }
        {
            var Q0;
            Q0=makeQuery(id+"F1.opExtrude","CAP_FACE",FACE,{"disambiguationData":[OSD([sQuery(id+"F0.wireOp",EDGE,"E0.bottom"),sQuery(id+"F0.wireOp",EDGE,"E0.top"),sQuery(id+"F0.wireOp",EDGE,"E0.left"),sQuery(id+"F0.wireOp",EDGE,"E0.right")])],"isStart":true});
            var sketch = newSketch(context, id + "F18", { "sketchPlane" : qUnion([Q0])});
            skArc(sketch, "E92", {"start": v(0, 28.58) * mm, "mid": v(-28.58, 0) * mm, "end": v(0, -28.58) * mm});
            skLineSegment(sketch, "E93", {"start": v(0, -28.58) * mm, "end": v(0, 28.58) * mm});
            skSolve(sketch);
        }
        {
            var Q0;
            Q0=makeQuery(id+"F18.imprint","IMPRINT",FACE,{"disambiguationData":[TD([[makeQuery(id+"F18.imprint","IMPRINT",EDGE,{"derivedFrom":sQuery(id+"F18.wireOp",EDGE,"E92")}),1.0]])]});
            extrude(context, id + "F19", {"entities" : qUnion([Q0]), "operationType" : NewBodyOperationType.ADD, "depth" : 2.54 * mm});
        }
        {
            var Q0;
            Q0=makeQuery(id+"F19.opExtrude","CAP_EDGE",EDGE,{"disambiguationData":[OSD([sQuery(id+"F18.wireOp",EDGE,"E92")])],"isStart":false});
            fillet(context, id + "F20", {"entities" : qUnion([Q0]), "radius" : 5.08 * mm, "tangentPropagation" : true, "allowEdgeOverflow" : false});
        }
        {
            var Q0;
            Q0=makeQuery(id+"F1.opExtrude","CAP_FACE",FACE,{"disambiguationData":[OSD([sQuery(id+"F0.wireOp",EDGE,"E0.bottom"),sQuery(id+"F0.wireOp",EDGE,"E0.top"),sQuery(id+"F0.wireOp",EDGE,"E0.left"),sQuery(id+"F0.wireOp",EDGE,"E0.right")])],"isStart":false});
            var sketch = newSketch(context, id + "F21", { "sketchPlane" : qUnion([Q0])});
            skLineSegment(sketch, "E94", {"start": v(-50.8, 38.1) * mm, "end": v(-50.8, -58.45) * mm});
            skLineSegment(sketch, "E95", {"start": v(-50.8, -58.45) * mm, "end": v(0, -58.45) * mm});
            skLineSegment(sketch, "E96", {"start": v(0, -58.45) * mm, "end": v(0, 53.65) * mm});
            skLineSegment(sketch, "E97", {"start": v(0, 53.65) * mm, "end": v(-50.8, 53.65) * mm});
            skLineSegment(sketch, "E98", {"start": v(-50.8, 53.65) * mm, "end": v(-50.8, 38.1) * mm});
            skSolve(sketch);
        }
        {
            var Q0;
            {var subQ5=sQuery(id+"F21.wireOp",EDGE,"E97");Q0=makeQuery(id+"F21.imprint","IMPRINT",FACE,{"disambiguationData":[TD([[makeQuery(id+"F21.imprint","IMPRINT",EDGE,{"derivedFrom":subQ5}),1.0]])]});}
            var Q1;
            {var subQ6=sQuery(id+"F21.wireOp",EDGE,"E95");Q1=makeQuery(id+"F21.imprint","IMPRINT",FACE,{"disambiguationData":[TD([[makeQuery(id+"F21.imprint","IMPRINT",EDGE,{"derivedFrom":subQ6}),1.0]])]});}
            var Q2;
            {var subQ0=sQuery(id+"F0.wireOp",EDGE,"E0.top");var subQ1=sQuery(id+"F0.wireOp",EDGE,"E0.bottom");var subQ2=makeQuery(id+"F1.opExtrude","CAP_FACE",FACE,{"disambiguationData":[OSD([subQ1,subQ0,sQuery(id+"F0.wireOp",EDGE,"E0.left"),sQuery(id+"F0.wireOp",EDGE,"E0.right")])],"isStart":false});var subQ6=sQuery(id+"F21.wireOp",EDGE,"E96");var subQ8=makeQuery(id+"F2.opChamfer","BLEND_EDGE",EDGE,{"blendedFrom":[makeQuery(id+"F1.opExtrude","CAP_EDGE",EDGE,{"disambiguationData":[OSD([subQ1])],"isStart":false}),subQ2],"blendedInto":[subQ2]});var subQ10=makeQuery(id+"F21.imprint","INTERSECT",VERTEX,{"derivedFrom":[subQ8,subQ6]});Q2=makeQuery(id+"F21.imprint","IMPRINT",FACE,{"disambiguationData":[TD([[makeQuery(id+"F21.imprint","IMPRINT",EDGE,{"disambiguationData":[TD([[subQ10,-1.0]])],"derivedFrom":subQ6}),1.0]])]});}
            extrude(context, id + "F22", {"entities" : qUnion([Q0, Q1, Q2]), "operationType" : NewBodyOperationType.REMOVE, "oppositeDirection" : true, "depth" : 2.54 * mm});
        }
        {
            var Q0;
            {var subQ0=sQuery(id+"F0.wireOp",EDGE,"E0.top");Q0=makeQuery(id+"F2.opChamfer","BLEND_FACE",FACE,{"disambiguationData":[OSD([subQ0]),TDD([makeQuery(id+"F1.opExtrude","CAP_EDGE",EDGE,{"disambiguationData":[OSD([subQ0])],"isStart":false})])]});}
            var sketch = newSketch(context, id + "F23", { "sketchPlane" : qUnion([Q0])});
            skLineSegment(sketch, "E99.bottom", {"start": v(50.8, 49.59) * mm, "end": v(45.72, 49.59) * mm});
            skLineSegment(sketch, "E99.top", {"start": v(49.53, 34.96) * mm, "end": v(47, 34.96) * mm});
            skLineSegment(sketch, "E99.left", {"start": v(50.8, 49.59) * mm, "end": v(50.8, 36.23) * mm});
            skLineSegment(sketch, "E99.right", {"start": v(45.72, 49.59) * mm, "end": v(45.72, 36.23) * mm});
            skPoint(sketch, "E100.visualSharp", {"position": v(50.8, 34.96) * mm});
            skArc(sketch, "E100.filletArc", {"start": v(49.53, 34.96) * mm, "mid": v(50.43, 35.33) * mm, "end": v(50.8, 36.23) * mm});
            skPoint(sketch, "E101.visualSharp", {"position": v(45.72, 34.96) * mm});
            skArc(sketch, "E101.filletArc", {"start": v(45.72, 36.23) * mm, "mid": v(46.1, 35.33) * mm, "end": v(47, 34.96) * mm});
            skSolve(sketch);
        }
        {
            var Q0;
            Q0=makeQuery(id+"F23.imprint","IMPRINT",FACE,{"disambiguationData":[TD([[makeQuery(id+"F23.imprint","IMPRINT",EDGE,{"derivedFrom":sQuery(id+"F23.wireOp",EDGE,"E99.top")}),-1.0]])]});
            var Q1;
            {var subQ5=sQuery(id+"F23.wireOp",EDGE,"E99.bottom");Q1=makeQuery(id+"F23.imprint","IMPRINT",FACE,{"disambiguationData":[TD([[makeQuery(id+"F23.imprint","IMPRINT",EDGE,{"derivedFrom":subQ5}),1.0]])]});}
            extrude(context, id + "F24", {"entities" : qUnion([Q0, Q1]), "operationType" : NewBodyOperationType.REMOVE, "oppositeDirection" : true, "depth" : 1.27 * mm});
        }
        {
            var Q0;
            {var subQ0=sQuery(id+"F0.wireOp",EDGE,"E0.bottom");Q0=makeQuery(id+"F2.opChamfer","BLEND_FACE",FACE,{"disambiguationData":[OSD([subQ0]),TDD([makeQuery(id+"F1.opExtrude","CAP_EDGE",EDGE,{"disambiguationData":[OSD([subQ0])],"isStart":false})])]});}
            var sketch = newSketch(context, id + "F25", { "sketchPlane" : qUnion([Q0])});
            skLineSegment(sketch, "E102.bottom", {"start": v(-50.8, 46.23) * mm, "end": v(-45.72, 46.23) * mm});
            skLineSegment(sketch, "E102.top", {"start": v(-49.53, 34.96) * mm, "end": v(-46.99, 34.96) * mm});
            skLineSegment(sketch, "E102.left", {"start": v(-50.8, 46.23) * mm, "end": v(-50.8, 36.23) * mm});
            skLineSegment(sketch, "E102.right", {"start": v(-45.72, 46.23) * mm, "end": v(-45.72, 36.23) * mm});
            skPoint(sketch, "E103.visualSharp", {"position": v(-50.8, 34.96) * mm});
            skArc(sketch, "E103.filletArc", {"start": v(-50.8, 36.23) * mm, "mid": v(-50.43, 35.33) * mm, "end": v(-49.53, 34.96) * mm});
            skPoint(sketch, "E104.visualSharp", {"position": v(-45.72, 34.96) * mm});
            skArc(sketch, "E104.filletArc", {"start": v(-46.99, 34.96) * mm, "mid": v(-46.1, 35.33) * mm, "end": v(-45.72, 36.23) * mm});
            skSolve(sketch);
        }
        {
            var Q0;
            Q0=makeQuery(id+"F25.imprint","IMPRINT",FACE,{"disambiguationData":[TD([[makeQuery(id+"F25.imprint","IMPRINT",EDGE,{"derivedFrom":sQuery(id+"F25.wireOp",EDGE,"E102.top")}),1.0]])]});
            var Q1;
            {var subQ7=sQuery(id+"F25.wireOp",EDGE,"E102.bottom");Q1=makeQuery(id+"F25.imprint","IMPRINT",FACE,{"disambiguationData":[TD([[makeQuery(id+"F25.imprint","IMPRINT",EDGE,{"derivedFrom":subQ7}),-1.0]])]});}
            extrude(context, id + "F26", {"entities" : qUnion([Q0, Q1]), "operationType" : NewBodyOperationType.REMOVE, "oppositeDirection" : true, "depth" : 1.27 * mm});
        }
        {
            var Q0;
            Q0=makeQuery(id+"F22.boolean.opBoolean","COPY",FACE,{"derivedFrom":makeQuery(id+"F22.opExtrude","CAP_FACE",FACE,{"disambiguationData":[OSD([sQuery(id+"F21.wireOp",EDGE,"E94"),sQuery(id+"F21.wireOp",EDGE,"E95"),sQuery(id+"F21.wireOp",EDGE,"E96"),sQuery(id+"F21.wireOp",EDGE,"E97"),sQuery(id+"F21.wireOp",EDGE,"E98")])],"isStart":false})});
            var sketch = newSketch(context, id + "F27", { "sketchPlane" : qUnion([Q0])});
            skCircle(sketch, "E105", {"center": v(0, 0) * mm, "radius": 19.05 * mm});
            skSolve(sketch);
        }
        {
            var Q0;
            {var subQ0=makeQuery(id+"F22.boolean.opBoolean","COPY",EDGE,{"derivedFrom":makeQuery(id+"F22.opExtrude","CAP_EDGE",EDGE,{"disambiguationData":[OSD([sQuery(id+"F21.wireOp",EDGE,"E96")])],"isStart":false})});var subQ1=sQuery(id+"F27.wireOp",EDGE,"E105");var subQ3=makeQuery(id+"F27.imprint","INTERSECT",VERTEX,{"disambiguationData":[OD(0.0)],"derivedFrom":[subQ0,subQ1]});Q0=makeQuery(id+"F27.imprint","IMPRINT",FACE,{"disambiguationData":[TD([[makeQuery(id+"F27.imprint","IMPRINT",EDGE,{"disambiguationData":[TD([[subQ3,-1.0]])],"derivedFrom":subQ1}),1.0]])]});}
            var Q1;
            {var subQ0=makeQuery(id+"F22.boolean.opBoolean","COPY",EDGE,{"derivedFrom":makeQuery(id+"F22.opExtrude","CAP_EDGE",EDGE,{"disambiguationData":[OSD([sQuery(id+"F21.wireOp",EDGE,"E96")])],"isStart":false})});var subQ1=sQuery(id+"F27.wireOp",EDGE,"E105");var subQ3=makeQuery(id+"F27.imprint","INTERSECT",VERTEX,{"disambiguationData":[OD(0.0)],"derivedFrom":[subQ0,subQ1]});Q1=makeQuery(id+"F27.imprint","IMPRINT",FACE,{"disambiguationData":[TD([[makeQuery(id+"F27.imprint","IMPRINT",EDGE,{"disambiguationData":[TD([[subQ3,1.0]])],"derivedFrom":subQ1}),1.0]])]});}
            extrude(context, id + "F28", {"entities" : qUnion([Q0, Q1]), "operationType" : NewBodyOperationType.REMOVE, "oppositeDirection" : true, "depth" : 63.5 * mm});
        }
        {
            var Q0;
            Q0=makeQuery(id+"F1.opExtrude","SWEPT_BODY",BODY,{"disambiguationData":[OSD([sQuery(id+"F0.wireOp",EDGE,"E0.bottom"),sQuery(id+"F0.wireOp",EDGE,"E0.top"),sQuery(id+"F0.wireOp",EDGE,"E0.left"),sQuery(id+"F0.wireOp",EDGE,"E0.right")])]});
            var Q1;
            Q1=makeQuery(id+"F17.opPattern","COPY",BODY,{"derivedFrom":makeQuery(id+"F9.opExtrude","SWEPT_BODY",BODY,{"disambiguationData":[OSD([sQuery(id+"F8.wireOp",EDGE,"E8"),sQuery(id+"F8.wireOp",EDGE,"E9"),sQuery(id+"F8.wireOp",EDGE,"E10"),sQuery(id+"F8.wireOp",EDGE,"E11"),sQuery(id+"F8.wireOp",EDGE,"E12.filletArc"),sQuery(id+"F8.wireOp",EDGE,"E13.filletArc"),sQuery(id+"F8.wireOp",EDGE,"E14.0"),sQuery(id+"F8.wireOp",EDGE,"E14.1"),sQuery(id+"F8.wireOp",EDGE,"E14.2"),sQuery(id+"F8.wireOp",EDGE,"E15"),sQuery(id+"F8.wireOp",EDGE,"E16"),sQuery(id+"F8.wireOp",EDGE,"E17"),sQuery(id+"F8.wireOp",EDGE,"E18"),sQuery(id+"F8.wireOp",EDGE,"E19.0"),sQuery(id+"F8.wireOp",EDGE,"E19.1"),sQuery(id+"F8.wireOp",EDGE,"E19.2"),sQuery(id+"F8.wireOp",EDGE,"E20"),sQuery(id+"F8.wireOp",EDGE,"E21.trimOffspring"),sQuery(id+"F8.wireOp",EDGE,"E22"),sQuery(id+"F8.wireOp",EDGE,"E23.trimOffspring"),sQuery(id+"F8.wireOp",EDGE,"E24.trimOffspring"),sQuery(id+"F8.wireOp",EDGE,"E25"),sQuery(id+"F8.wireOp",EDGE,"E26"),sQuery(id+"F8.wireOp",EDGE,"E27"),sQuery(id+"F8.wireOp",EDGE,"E28.trimOffspring"),sQuery(id+"F8.wireOp",EDGE,"E29"),sQuery(id+"F8.wireOp",EDGE,"E30"),sQuery(id+"F8.wireOp",EDGE,"E31"),sQuery(id+"F8.wireOp",EDGE,"E32"),sQuery(id+"F8.wireOp",EDGE,"E33"),sQuery(id+"F8.wireOp",EDGE,"E34"),sQuery(id+"F8.wireOp",EDGE,"E35.trimOffspring"),sQuery(id+"F8.wireOp",EDGE,"E36"),sQuery(id+"F8.wireOp",EDGE,"E37"),sQuery(id+"F8.wireOp",EDGE,"E38"),sQuery(id+"F8.wireOp",EDGE,"E39"),sQuery(id+"F8.wireOp",EDGE,"E40"),sQuery(id+"F8.wireOp",EDGE,"E41"),sQuery(id+"F8.wireOp",EDGE,"E42.trimOffspring"),sQuery(id+"F8.wireOp",EDGE,"E43"),sQuery(id+"F8.wireOp",EDGE,"E44"),sQuery(id+"F8.wireOp",EDGE,"E45"),sQuery(id+"F8.wireOp",EDGE,"E46.trimOffspring"),sQuery(id+"F8.wireOp",EDGE,"E47"),sQuery(id+"F8.wireOp",EDGE,"E48"),sQuery(id+"F8.wireOp",EDGE,"E49"),sQuery(id+"F8.wireOp",EDGE,"E50"),sQuery(id+"F8.wireOp",EDGE,"E51"),sQuery(id+"F8.wireOp",EDGE,"E52"),sQuery(id+"F8.wireOp",EDGE,"E53"),sQuery(id+"F8.wireOp",EDGE,"E54.trimOffspring"),sQuery(id+"F8.wireOp",EDGE,"E55.trimOffspring"),sQuery(id+"F8.wireOp",EDGE,"E56.trimOffspring"),sQuery(id+"F8.wireOp",EDGE,"E57.trimOffspring"),sQuery(id+"F8.wireOp",EDGE,"E58.trimOffspring"),sQuery(id+"F8.wireOp",EDGE,"E59"),sQuery(id+"F8.wireOp",EDGE,"E60"),sQuery(id+"F8.wireOp",EDGE,"E61"),sQuery(id+"F8.wireOp",EDGE,"E62"),sQuery(id+"F8.wireOp",EDGE,"E63.trimOffspring"),sQuery(id+"F8.wireOp",EDGE,"E64"),sQuery(id+"F8.wireOp",EDGE,"E65"),sQuery(id+"F8.wireOp",EDGE,"E66"),sQuery(id+"F8.wireOp",EDGE,"E67"),sQuery(id+"F8.wireOp",EDGE,"E68"),sQuery(id+"F8.wireOp",EDGE,"E69"),sQuery(id+"F8.wireOp",EDGE,"E70"),sQuery(id+"F8.wireOp",EDGE,"E71"),sQuery(id+"F8.wireOp",EDGE,"E72"),sQuery(id+"F8.wireOp",EDGE,"E73.trimOffspring"),sQuery(id+"F8.wireOp",EDGE,"E74.trimOffspring"),sQuery(id+"F8.wireOp",EDGE,"E75.trimOffspring"),sQuery(id+"F8.wireOp",EDGE,"E76.trimOffspring"),sQuery(id+"F8.wireOp",EDGE,"E77"),sQuery(id+"F8.wireOp",EDGE,"E78"),sQuery(id+"F8.wireOp",EDGE,"E79"),sQuery(id+"F8.wireOp",EDGE,"E80"),sQuery(id+"F8.wireOp",EDGE,"E81.trimOffspring"),sQuery(id+"F8.wireOp",EDGE,"E87.0.MirrorCS"),sQuery(id+"F8.wireOp",EDGE,"E87.1.MirrorCS"),sQuery(id+"F8.wireOp",EDGE,"E87.2.MirrorCS"),sQuery(id+"F8.wireOp",EDGE,"E87.3.MirrorCS"),sQuery(id+"F8.wireOp",EDGE,"E87.5.MirrorCS"),sQuery(id+"F8.wireOp",EDGE,"E87.6.MirrorCS"),sQuery(id+"F8.wireOp",EDGE,"E87.7.MirrorCS"),sQuery(id+"F8.wireOp",EDGE,"E87.8.MirrorCS"),sQuery(id+"F8.wireOp",EDGE,"E87.9.MirrorCS"),sQuery(id+"F8.wireOp",EDGE,"E87.10.MirrorCS"),sQuery(id+"F8.wireOp",EDGE,"E87.11.MirrorCS"),sQuery(id+"F8.wireOp",EDGE,"E87.12.MirrorCS"),sQuery(id+"F8.wireOp",EDGE,"E87.14.MirrorCS"),sQuery(id+"F8.wireOp",EDGE,"E87.15.MirrorCS"),sQuery(id+"F8.wireOp",EDGE,"E87.16.MirrorCS"),sQuery(id+"F8.wireOp",EDGE,"E87.17.MirrorCS"),sQuery(id+"F8.wireOp",EDGE,"E87.18.MirrorCS"),sQuery(id+"F8.wireOp",EDGE,"E87.19.MirrorCS"),sQuery(id+"F8.wireOp",EDGE,"E87.20.MirrorCS"),sQuery(id+"F8.wireOp",EDGE,"E87.21.MirrorCS"),sQuery(id+"F8.wireOp",EDGE,"E87.23.MirrorCS"),sQuery(id+"F8.wireOp",EDGE,"E87.24.MirrorCS"),sQuery(id+"F8.wireOp",EDGE,"E87.25.MirrorCS"),sQuery(id+"F8.wireOp",EDGE,"E87.26.MirrorCS"),sQuery(id+"F8.wireOp",EDGE,"E87.27.MirrorCS"),sQuery(id+"F8.wireOp",EDGE,"E87.28.MirrorCS"),sQuery(id+"F8.wireOp",EDGE,"E87.29.MirrorCS"),sQuery(id+"F8.wireOp",EDGE,"E87.30.MirrorCS"),sQuery(id+"F8.wireOp",EDGE,"E87.32.MirrorCS"),sQuery(id+"F8.wireOp",EDGE,"E87.34.MirrorCS"),sQuery(id+"F8.wireOp",EDGE,"E87.35.MirrorCS"),sQuery(id+"F8.wireOp",EDGE,"E87.36.MirrorCS"),sQuery(id+"F8.wireOp",EDGE,"E87.37.MirrorCS"),sQuery(id+"F8.wireOp",EDGE,"E87.38.MirrorCS"),sQuery(id+"F8.wireOp",EDGE,"E87.39.MirrorCS"),sQuery(id+"F8.wireOp",EDGE,"E87.40.MirrorCS"),sQuery(id+"F8.wireOp",EDGE,"E87.41.MirrorCS"),sQuery(id+"F8.wireOp",EDGE,"E87.42.MirrorCS"),sQuery(id+"F8.wireOp",EDGE,"E87.43.MirrorCS"),sQuery(id+"F8.wireOp",EDGE,"E87.44.MirrorCS"),sQuery(id+"F8.wireOp",EDGE,"E87.45.MirrorCS"),sQuery(id+"F8.wireOp",EDGE,"E87.46.MirrorCS"),sQuery(id+"F8.wireOp",EDGE,"E87.47.MirrorCS"),sQuery(id+"F8.wireOp",EDGE,"E87.48.MirrorCS"),sQuery(id+"F8.wireOp",EDGE,"E87.49.MirrorCS"),sQuery(id+"F8.wireOp",EDGE,"E87.50.MirrorCS"),sQuery(id+"F8.wireOp",EDGE,"E87.51.MirrorCS"),sQuery(id+"F8.wireOp",EDGE,"E87.53.MirrorCS"),sQuery(id+"F8.wireOp",EDGE,"E87.54.MirrorCS"),sQuery(id+"F8.wireOp",EDGE,"E87.55.MirrorCS"),sQuery(id+"F8.wireOp",EDGE,"E87.56.MirrorCS"),sQuery(id+"F8.wireOp",EDGE,"E87.57.MirrorCS"),sQuery(id+"F8.wireOp",EDGE,"E87.58.MirrorCS"),sQuery(id+"F8.wireOp",EDGE,"E87.59.MirrorCS"),sQuery(id+"F8.wireOp",EDGE,"E87.60.MirrorCS"),sQuery(id+"F8.wireOp",EDGE,"E87.61.MirrorCS"),sQuery(id+"F8.wireOp",EDGE,"E87.62.MirrorCS"),sQuery(id+"F8.wireOp",EDGE,"E87.63.MirrorCS"),sQuery(id+"F8.wireOp",EDGE,"E87.65.MirrorCS"),sQuery(id+"F8.wireOp",EDGE,"E87.66.MirrorCS"),sQuery(id+"F8.wireOp",EDGE,"E87.67.MirrorCS"),sQuery(id+"F8.wireOp",EDGE,"E87.68.MirrorCS"),sQuery(id+"F8.wireOp",EDGE,"E87.69.MirrorCS"),sQuery(id+"F8.wireOp",EDGE,"E87.70.MirrorCS"),sQuery(id+"F8.wireOp",EDGE,"E87.71.MirrorCS"),sQuery(id+"F8.wireOp",EDGE,"E87.72.MirrorCS"),sQuery(id+"F8.wireOp",EDGE,"E87.73.MirrorCS"),sQuery(id+"F8.wireOp",EDGE,"E87.74.MirrorCS"),sQuery(id+"F8.wireOp",EDGE,"E87.75.MirrorCS"),sQuery(id+"F8.wireOp",EDGE,"E87.76.MirrorCS"),sQuery(id+"F8.wireOp",EDGE,"E87.77.MirrorCS"),sQuery(id+"F8.wireOp",EDGE,"E87.78.MirrorCS"),sQuery(id+"F8.wireOp",EDGE,"E87.79.MirrorCS"),sQuery(id+"F8.wireOp",EDGE,"E87.80.MirrorCS"),sQuery(id+"F8.wireOp",EDGE,"E87.81.MirrorCS"),sQuery(id+"F8.wireOp",EDGE,"E87.82.MirrorCS"),sQuery(id+"F8.wireOp",EDGE,"E87.83.MirrorCS"),sQuery(id+"F8.wireOp",EDGE,"E87.84.MirrorCS")])]}),"instanceName":"1"});
            var Q2;
            Q2=makeQuery(id+"F17.opPattern","COPY",BODY,{"derivedFrom":makeQuery(id+"F9.opExtrude","SWEPT_BODY",BODY,{"disambiguationData":[OSD([sQuery(id+"F8.wireOp",EDGE,"E82"),sQuery(id+"F8.wireOp",EDGE,"E83"),sQuery(id+"F8.wireOp",EDGE,"E84"),sQuery(id+"F8.wireOp",EDGE,"E85"),sQuery(id+"F8.wireOp",EDGE,"E86"),sQuery(id+"F8.wireOp",EDGE,"E87.13.MirrorCS"),sQuery(id+"F8.wireOp",EDGE,"E87.31.MirrorCS"),sQuery(id+"F8.wireOp",EDGE,"E87.33.MirrorCS"),sQuery(id+"F8.wireOp",EDGE,"E87.64.MirrorCS"),sQuery(id+"F8.wireOp",EDGE,"E87.22.MirrorCS")])]}),"instanceName":"1"});
            var Q3;
            Q3=makeQuery(id+"F9.opExtrude","SWEPT_BODY",BODY,{"disambiguationData":[OSD([sQuery(id+"F8.wireOp",EDGE,"E8"),sQuery(id+"F8.wireOp",EDGE,"E9"),sQuery(id+"F8.wireOp",EDGE,"E10"),sQuery(id+"F8.wireOp",EDGE,"E11"),sQuery(id+"F8.wireOp",EDGE,"E12.filletArc"),sQuery(id+"F8.wireOp",EDGE,"E13.filletArc"),sQuery(id+"F8.wireOp",EDGE,"E14.0"),sQuery(id+"F8.wireOp",EDGE,"E14.1"),sQuery(id+"F8.wireOp",EDGE,"E14.2"),sQuery(id+"F8.wireOp",EDGE,"E15"),sQuery(id+"F8.wireOp",EDGE,"E16"),sQuery(id+"F8.wireOp",EDGE,"E17"),sQuery(id+"F8.wireOp",EDGE,"E18"),sQuery(id+"F8.wireOp",EDGE,"E19.0"),sQuery(id+"F8.wireOp",EDGE,"E19.1"),sQuery(id+"F8.wireOp",EDGE,"E19.2"),sQuery(id+"F8.wireOp",EDGE,"E20"),sQuery(id+"F8.wireOp",EDGE,"E21.trimOffspring"),sQuery(id+"F8.wireOp",EDGE,"E22"),sQuery(id+"F8.wireOp",EDGE,"E23.trimOffspring"),sQuery(id+"F8.wireOp",EDGE,"E24.trimOffspring"),sQuery(id+"F8.wireOp",EDGE,"E25"),sQuery(id+"F8.wireOp",EDGE,"E26"),sQuery(id+"F8.wireOp",EDGE,"E27"),sQuery(id+"F8.wireOp",EDGE,"E28.trimOffspring"),sQuery(id+"F8.wireOp",EDGE,"E29"),sQuery(id+"F8.wireOp",EDGE,"E30"),sQuery(id+"F8.wireOp",EDGE,"E31"),sQuery(id+"F8.wireOp",EDGE,"E32"),sQuery(id+"F8.wireOp",EDGE,"E33"),sQuery(id+"F8.wireOp",EDGE,"E34"),sQuery(id+"F8.wireOp",EDGE,"E35.trimOffspring"),sQuery(id+"F8.wireOp",EDGE,"E36"),sQuery(id+"F8.wireOp",EDGE,"E37"),sQuery(id+"F8.wireOp",EDGE,"E38"),sQuery(id+"F8.wireOp",EDGE,"E39"),sQuery(id+"F8.wireOp",EDGE,"E40"),sQuery(id+"F8.wireOp",EDGE,"E41"),sQuery(id+"F8.wireOp",EDGE,"E42.trimOffspring"),sQuery(id+"F8.wireOp",EDGE,"E43"),sQuery(id+"F8.wireOp",EDGE,"E44"),sQuery(id+"F8.wireOp",EDGE,"E45"),sQuery(id+"F8.wireOp",EDGE,"E46.trimOffspring"),sQuery(id+"F8.wireOp",EDGE,"E47"),sQuery(id+"F8.wireOp",EDGE,"E48"),sQuery(id+"F8.wireOp",EDGE,"E49"),sQuery(id+"F8.wireOp",EDGE,"E50"),sQuery(id+"F8.wireOp",EDGE,"E51"),sQuery(id+"F8.wireOp",EDGE,"E52"),sQuery(id+"F8.wireOp",EDGE,"E53"),sQuery(id+"F8.wireOp",EDGE,"E54.trimOffspring"),sQuery(id+"F8.wireOp",EDGE,"E55.trimOffspring"),sQuery(id+"F8.wireOp",EDGE,"E56.trimOffspring"),sQuery(id+"F8.wireOp",EDGE,"E57.trimOffspring"),sQuery(id+"F8.wireOp",EDGE,"E58.trimOffspring"),sQuery(id+"F8.wireOp",EDGE,"E59"),sQuery(id+"F8.wireOp",EDGE,"E60"),sQuery(id+"F8.wireOp",EDGE,"E61"),sQuery(id+"F8.wireOp",EDGE,"E62"),sQuery(id+"F8.wireOp",EDGE,"E63.trimOffspring"),sQuery(id+"F8.wireOp",EDGE,"E64"),sQuery(id+"F8.wireOp",EDGE,"E65"),sQuery(id+"F8.wireOp",EDGE,"E66"),sQuery(id+"F8.wireOp",EDGE,"E67"),sQuery(id+"F8.wireOp",EDGE,"E68"),sQuery(id+"F8.wireOp",EDGE,"E69"),sQuery(id+"F8.wireOp",EDGE,"E70"),sQuery(id+"F8.wireOp",EDGE,"E71"),sQuery(id+"F8.wireOp",EDGE,"E72"),sQuery(id+"F8.wireOp",EDGE,"E73.trimOffspring"),sQuery(id+"F8.wireOp",EDGE,"E74.trimOffspring"),sQuery(id+"F8.wireOp",EDGE,"E75.trimOffspring"),sQuery(id+"F8.wireOp",EDGE,"E76.trimOffspring"),sQuery(id+"F8.wireOp",EDGE,"E77"),sQuery(id+"F8.wireOp",EDGE,"E78"),sQuery(id+"F8.wireOp",EDGE,"E79"),sQuery(id+"F8.wireOp",EDGE,"E80"),sQuery(id+"F8.wireOp",EDGE,"E81.trimOffspring"),sQuery(id+"F8.wireOp",EDGE,"E87.0.MirrorCS"),sQuery(id+"F8.wireOp",EDGE,"E87.1.MirrorCS"),sQuery(id+"F8.wireOp",EDGE,"E87.2.MirrorCS"),sQuery(id+"F8.wireOp",EDGE,"E87.3.MirrorCS"),sQuery(id+"F8.wireOp",EDGE,"E87.5.MirrorCS"),sQuery(id+"F8.wireOp",EDGE,"E87.6.MirrorCS"),sQuery(id+"F8.wireOp",EDGE,"E87.7.MirrorCS"),sQuery(id+"F8.wireOp",EDGE,"E87.8.MirrorCS"),sQuery(id+"F8.wireOp",EDGE,"E87.9.MirrorCS"),sQuery(id+"F8.wireOp",EDGE,"E87.10.MirrorCS"),sQuery(id+"F8.wireOp",EDGE,"E87.11.MirrorCS"),sQuery(id+"F8.wireOp",EDGE,"E87.12.MirrorCS"),sQuery(id+"F8.wireOp",EDGE,"E87.14.MirrorCS"),sQuery(id+"F8.wireOp",EDGE,"E87.15.MirrorCS"),sQuery(id+"F8.wireOp",EDGE,"E87.16.MirrorCS"),sQuery(id+"F8.wireOp",EDGE,"E87.17.MirrorCS"),sQuery(id+"F8.wireOp",EDGE,"E87.18.MirrorCS"),sQuery(id+"F8.wireOp",EDGE,"E87.19.MirrorCS"),sQuery(id+"F8.wireOp",EDGE,"E87.20.MirrorCS"),sQuery(id+"F8.wireOp",EDGE,"E87.21.MirrorCS"),sQuery(id+"F8.wireOp",EDGE,"E87.23.MirrorCS"),sQuery(id+"F8.wireOp",EDGE,"E87.24.MirrorCS"),sQuery(id+"F8.wireOp",EDGE,"E87.25.MirrorCS"),sQuery(id+"F8.wireOp",EDGE,"E87.26.MirrorCS"),sQuery(id+"F8.wireOp",EDGE,"E87.27.MirrorCS"),sQuery(id+"F8.wireOp",EDGE,"E87.28.MirrorCS"),sQuery(id+"F8.wireOp",EDGE,"E87.29.MirrorCS"),sQuery(id+"F8.wireOp",EDGE,"E87.30.MirrorCS"),sQuery(id+"F8.wireOp",EDGE,"E87.32.MirrorCS"),sQuery(id+"F8.wireOp",EDGE,"E87.34.MirrorCS"),sQuery(id+"F8.wireOp",EDGE,"E87.35.MirrorCS"),sQuery(id+"F8.wireOp",EDGE,"E87.36.MirrorCS"),sQuery(id+"F8.wireOp",EDGE,"E87.37.MirrorCS"),sQuery(id+"F8.wireOp",EDGE,"E87.38.MirrorCS"),sQuery(id+"F8.wireOp",EDGE,"E87.39.MirrorCS"),sQuery(id+"F8.wireOp",EDGE,"E87.40.MirrorCS"),sQuery(id+"F8.wireOp",EDGE,"E87.41.MirrorCS"),sQuery(id+"F8.wireOp",EDGE,"E87.42.MirrorCS"),sQuery(id+"F8.wireOp",EDGE,"E87.43.MirrorCS"),sQuery(id+"F8.wireOp",EDGE,"E87.44.MirrorCS"),sQuery(id+"F8.wireOp",EDGE,"E87.45.MirrorCS"),sQuery(id+"F8.wireOp",EDGE,"E87.46.MirrorCS"),sQuery(id+"F8.wireOp",EDGE,"E87.47.MirrorCS"),sQuery(id+"F8.wireOp",EDGE,"E87.48.MirrorCS"),sQuery(id+"F8.wireOp",EDGE,"E87.49.MirrorCS"),sQuery(id+"F8.wireOp",EDGE,"E87.50.MirrorCS"),sQuery(id+"F8.wireOp",EDGE,"E87.51.MirrorCS"),sQuery(id+"F8.wireOp",EDGE,"E87.53.MirrorCS"),sQuery(id+"F8.wireOp",EDGE,"E87.54.MirrorCS"),sQuery(id+"F8.wireOp",EDGE,"E87.55.MirrorCS"),sQuery(id+"F8.wireOp",EDGE,"E87.56.MirrorCS"),sQuery(id+"F8.wireOp",EDGE,"E87.57.MirrorCS"),sQuery(id+"F8.wireOp",EDGE,"E87.58.MirrorCS"),sQuery(id+"F8.wireOp",EDGE,"E87.59.MirrorCS"),sQuery(id+"F8.wireOp",EDGE,"E87.60.MirrorCS"),sQuery(id+"F8.wireOp",EDGE,"E87.61.MirrorCS"),sQuery(id+"F8.wireOp",EDGE,"E87.62.MirrorCS"),sQuery(id+"F8.wireOp",EDGE,"E87.63.MirrorCS"),sQuery(id+"F8.wireOp",EDGE,"E87.65.MirrorCS"),sQuery(id+"F8.wireOp",EDGE,"E87.66.MirrorCS"),sQuery(id+"F8.wireOp",EDGE,"E87.67.MirrorCS"),sQuery(id+"F8.wireOp",EDGE,"E87.68.MirrorCS"),sQuery(id+"F8.wireOp",EDGE,"E87.69.MirrorCS"),sQuery(id+"F8.wireOp",EDGE,"E87.70.MirrorCS"),sQuery(id+"F8.wireOp",EDGE,"E87.71.MirrorCS"),sQuery(id+"F8.wireOp",EDGE,"E87.72.MirrorCS"),sQuery(id+"F8.wireOp",EDGE,"E87.73.MirrorCS"),sQuery(id+"F8.wireOp",EDGE,"E87.74.MirrorCS"),sQuery(id+"F8.wireOp",EDGE,"E87.75.MirrorCS"),sQuery(id+"F8.wireOp",EDGE,"E87.76.MirrorCS"),sQuery(id+"F8.wireOp",EDGE,"E87.77.MirrorCS"),sQuery(id+"F8.wireOp",EDGE,"E87.78.MirrorCS"),sQuery(id+"F8.wireOp",EDGE,"E87.79.MirrorCS"),sQuery(id+"F8.wireOp",EDGE,"E87.80.MirrorCS"),sQuery(id+"F8.wireOp",EDGE,"E87.81.MirrorCS"),sQuery(id+"F8.wireOp",EDGE,"E87.82.MirrorCS"),sQuery(id+"F8.wireOp",EDGE,"E87.83.MirrorCS"),sQuery(id+"F8.wireOp",EDGE,"E87.84.MirrorCS")])]});
            var Q4;
            Q4=makeQuery(id+"F9.opExtrude","SWEPT_BODY",BODY,{"disambiguationData":[OSD([sQuery(id+"F8.wireOp",EDGE,"E82"),sQuery(id+"F8.wireOp",EDGE,"E83"),sQuery(id+"F8.wireOp",EDGE,"E84"),sQuery(id+"F8.wireOp",EDGE,"E85"),sQuery(id+"F8.wireOp",EDGE,"E86"),sQuery(id+"F8.wireOp",EDGE,"E87.13.MirrorCS"),sQuery(id+"F8.wireOp",EDGE,"E87.31.MirrorCS"),sQuery(id+"F8.wireOp",EDGE,"E87.33.MirrorCS"),sQuery(id+"F8.wireOp",EDGE,"E87.64.MirrorCS"),sQuery(id+"F8.wireOp",EDGE,"E87.22.MirrorCS")])]});
            var Q5;
            Q5=makeQuery(id+"F17.opPattern","COPY",BODY,{"derivedFrom":makeQuery(id+"F9.opExtrude","SWEPT_BODY",BODY,{"disambiguationData":[OSD([sQuery(id+"F8.wireOp",EDGE,"E8"),sQuery(id+"F8.wireOp",EDGE,"E9"),sQuery(id+"F8.wireOp",EDGE,"E10"),sQuery(id+"F8.wireOp",EDGE,"E11"),sQuery(id+"F8.wireOp",EDGE,"E12.filletArc"),sQuery(id+"F8.wireOp",EDGE,"E13.filletArc"),sQuery(id+"F8.wireOp",EDGE,"E14.0"),sQuery(id+"F8.wireOp",EDGE,"E14.1"),sQuery(id+"F8.wireOp",EDGE,"E14.2"),sQuery(id+"F8.wireOp",EDGE,"E15"),sQuery(id+"F8.wireOp",EDGE,"E16"),sQuery(id+"F8.wireOp",EDGE,"E17"),sQuery(id+"F8.wireOp",EDGE,"E18"),sQuery(id+"F8.wireOp",EDGE,"E19.0"),sQuery(id+"F8.wireOp",EDGE,"E19.1"),sQuery(id+"F8.wireOp",EDGE,"E19.2"),sQuery(id+"F8.wireOp",EDGE,"E20"),sQuery(id+"F8.wireOp",EDGE,"E21.trimOffspring"),sQuery(id+"F8.wireOp",EDGE,"E22"),sQuery(id+"F8.wireOp",EDGE,"E23.trimOffspring"),sQuery(id+"F8.wireOp",EDGE,"E24.trimOffspring"),sQuery(id+"F8.wireOp",EDGE,"E25"),sQuery(id+"F8.wireOp",EDGE,"E26"),sQuery(id+"F8.wireOp",EDGE,"E27"),sQuery(id+"F8.wireOp",EDGE,"E28.trimOffspring"),sQuery(id+"F8.wireOp",EDGE,"E29"),sQuery(id+"F8.wireOp",EDGE,"E30"),sQuery(id+"F8.wireOp",EDGE,"E31"),sQuery(id+"F8.wireOp",EDGE,"E32"),sQuery(id+"F8.wireOp",EDGE,"E33"),sQuery(id+"F8.wireOp",EDGE,"E34"),sQuery(id+"F8.wireOp",EDGE,"E35.trimOffspring"),sQuery(id+"F8.wireOp",EDGE,"E36"),sQuery(id+"F8.wireOp",EDGE,"E37"),sQuery(id+"F8.wireOp",EDGE,"E38"),sQuery(id+"F8.wireOp",EDGE,"E39"),sQuery(id+"F8.wireOp",EDGE,"E40"),sQuery(id+"F8.wireOp",EDGE,"E41"),sQuery(id+"F8.wireOp",EDGE,"E42.trimOffspring"),sQuery(id+"F8.wireOp",EDGE,"E43"),sQuery(id+"F8.wireOp",EDGE,"E44"),sQuery(id+"F8.wireOp",EDGE,"E45"),sQuery(id+"F8.wireOp",EDGE,"E46.trimOffspring"),sQuery(id+"F8.wireOp",EDGE,"E47"),sQuery(id+"F8.wireOp",EDGE,"E48"),sQuery(id+"F8.wireOp",EDGE,"E49"),sQuery(id+"F8.wireOp",EDGE,"E50"),sQuery(id+"F8.wireOp",EDGE,"E51"),sQuery(id+"F8.wireOp",EDGE,"E52"),sQuery(id+"F8.wireOp",EDGE,"E53"),sQuery(id+"F8.wireOp",EDGE,"E54.trimOffspring"),sQuery(id+"F8.wireOp",EDGE,"E55.trimOffspring"),sQuery(id+"F8.wireOp",EDGE,"E56.trimOffspring"),sQuery(id+"F8.wireOp",EDGE,"E57.trimOffspring"),sQuery(id+"F8.wireOp",EDGE,"E58.trimOffspring"),sQuery(id+"F8.wireOp",EDGE,"E59"),sQuery(id+"F8.wireOp",EDGE,"E60"),sQuery(id+"F8.wireOp",EDGE,"E61"),sQuery(id+"F8.wireOp",EDGE,"E62"),sQuery(id+"F8.wireOp",EDGE,"E63.trimOffspring"),sQuery(id+"F8.wireOp",EDGE,"E64"),sQuery(id+"F8.wireOp",EDGE,"E65"),sQuery(id+"F8.wireOp",EDGE,"E66"),sQuery(id+"F8.wireOp",EDGE,"E67"),sQuery(id+"F8.wireOp",EDGE,"E68"),sQuery(id+"F8.wireOp",EDGE,"E69"),sQuery(id+"F8.wireOp",EDGE,"E70"),sQuery(id+"F8.wireOp",EDGE,"E71"),sQuery(id+"F8.wireOp",EDGE,"E72"),sQuery(id+"F8.wireOp",EDGE,"E73.trimOffspring"),sQuery(id+"F8.wireOp",EDGE,"E74.trimOffspring"),sQuery(id+"F8.wireOp",EDGE,"E75.trimOffspring"),sQuery(id+"F8.wireOp",EDGE,"E76.trimOffspring"),sQuery(id+"F8.wireOp",EDGE,"E77"),sQuery(id+"F8.wireOp",EDGE,"E78"),sQuery(id+"F8.wireOp",EDGE,"E79"),sQuery(id+"F8.wireOp",EDGE,"E80"),sQuery(id+"F8.wireOp",EDGE,"E81.trimOffspring"),sQuery(id+"F8.wireOp",EDGE,"E87.0.MirrorCS"),sQuery(id+"F8.wireOp",EDGE,"E87.1.MirrorCS"),sQuery(id+"F8.wireOp",EDGE,"E87.2.MirrorCS"),sQuery(id+"F8.wireOp",EDGE,"E87.3.MirrorCS"),sQuery(id+"F8.wireOp",EDGE,"E87.5.MirrorCS"),sQuery(id+"F8.wireOp",EDGE,"E87.6.MirrorCS"),sQuery(id+"F8.wireOp",EDGE,"E87.7.MirrorCS"),sQuery(id+"F8.wireOp",EDGE,"E87.8.MirrorCS"),sQuery(id+"F8.wireOp",EDGE,"E87.9.MirrorCS"),sQuery(id+"F8.wireOp",EDGE,"E87.10.MirrorCS"),sQuery(id+"F8.wireOp",EDGE,"E87.11.MirrorCS"),sQuery(id+"F8.wireOp",EDGE,"E87.12.MirrorCS"),sQuery(id+"F8.wireOp",EDGE,"E87.14.MirrorCS"),sQuery(id+"F8.wireOp",EDGE,"E87.15.MirrorCS"),sQuery(id+"F8.wireOp",EDGE,"E87.16.MirrorCS"),sQuery(id+"F8.wireOp",EDGE,"E87.17.MirrorCS"),sQuery(id+"F8.wireOp",EDGE,"E87.18.MirrorCS"),sQuery(id+"F8.wireOp",EDGE,"E87.19.MirrorCS"),sQuery(id+"F8.wireOp",EDGE,"E87.20.MirrorCS"),sQuery(id+"F8.wireOp",EDGE,"E87.21.MirrorCS"),sQuery(id+"F8.wireOp",EDGE,"E87.23.MirrorCS"),sQuery(id+"F8.wireOp",EDGE,"E87.24.MirrorCS"),sQuery(id+"F8.wireOp",EDGE,"E87.25.MirrorCS"),sQuery(id+"F8.wireOp",EDGE,"E87.26.MirrorCS"),sQuery(id+"F8.wireOp",EDGE,"E87.27.MirrorCS"),sQuery(id+"F8.wireOp",EDGE,"E87.28.MirrorCS"),sQuery(id+"F8.wireOp",EDGE,"E87.29.MirrorCS"),sQuery(id+"F8.wireOp",EDGE,"E87.30.MirrorCS"),sQuery(id+"F8.wireOp",EDGE,"E87.32.MirrorCS"),sQuery(id+"F8.wireOp",EDGE,"E87.34.MirrorCS"),sQuery(id+"F8.wireOp",EDGE,"E87.35.MirrorCS"),sQuery(id+"F8.wireOp",EDGE,"E87.36.MirrorCS"),sQuery(id+"F8.wireOp",EDGE,"E87.37.MirrorCS"),sQuery(id+"F8.wireOp",EDGE,"E87.38.MirrorCS"),sQuery(id+"F8.wireOp",EDGE,"E87.39.MirrorCS"),sQuery(id+"F8.wireOp",EDGE,"E87.40.MirrorCS"),sQuery(id+"F8.wireOp",EDGE,"E87.41.MirrorCS"),sQuery(id+"F8.wireOp",EDGE,"E87.42.MirrorCS"),sQuery(id+"F8.wireOp",EDGE,"E87.43.MirrorCS"),sQuery(id+"F8.wireOp",EDGE,"E87.44.MirrorCS"),sQuery(id+"F8.wireOp",EDGE,"E87.45.MirrorCS"),sQuery(id+"F8.wireOp",EDGE,"E87.46.MirrorCS"),sQuery(id+"F8.wireOp",EDGE,"E87.47.MirrorCS"),sQuery(id+"F8.wireOp",EDGE,"E87.48.MirrorCS"),sQuery(id+"F8.wireOp",EDGE,"E87.49.MirrorCS"),sQuery(id+"F8.wireOp",EDGE,"E87.50.MirrorCS"),sQuery(id+"F8.wireOp",EDGE,"E87.51.MirrorCS"),sQuery(id+"F8.wireOp",EDGE,"E87.53.MirrorCS"),sQuery(id+"F8.wireOp",EDGE,"E87.54.MirrorCS"),sQuery(id+"F8.wireOp",EDGE,"E87.55.MirrorCS"),sQuery(id+"F8.wireOp",EDGE,"E87.56.MirrorCS"),sQuery(id+"F8.wireOp",EDGE,"E87.57.MirrorCS"),sQuery(id+"F8.wireOp",EDGE,"E87.58.MirrorCS"),sQuery(id+"F8.wireOp",EDGE,"E87.59.MirrorCS"),sQuery(id+"F8.wireOp",EDGE,"E87.60.MirrorCS"),sQuery(id+"F8.wireOp",EDGE,"E87.61.MirrorCS"),sQuery(id+"F8.wireOp",EDGE,"E87.62.MirrorCS"),sQuery(id+"F8.wireOp",EDGE,"E87.63.MirrorCS"),sQuery(id+"F8.wireOp",EDGE,"E87.65.MirrorCS"),sQuery(id+"F8.wireOp",EDGE,"E87.66.MirrorCS"),sQuery(id+"F8.wireOp",EDGE,"E87.67.MirrorCS"),sQuery(id+"F8.wireOp",EDGE,"E87.68.MirrorCS"),sQuery(id+"F8.wireOp",EDGE,"E87.69.MirrorCS"),sQuery(id+"F8.wireOp",EDGE,"E87.70.MirrorCS"),sQuery(id+"F8.wireOp",EDGE,"E87.71.MirrorCS"),sQuery(id+"F8.wireOp",EDGE,"E87.72.MirrorCS"),sQuery(id+"F8.wireOp",EDGE,"E87.73.MirrorCS"),sQuery(id+"F8.wireOp",EDGE,"E87.74.MirrorCS"),sQuery(id+"F8.wireOp",EDGE,"E87.75.MirrorCS"),sQuery(id+"F8.wireOp",EDGE,"E87.76.MirrorCS"),sQuery(id+"F8.wireOp",EDGE,"E87.77.MirrorCS"),sQuery(id+"F8.wireOp",EDGE,"E87.78.MirrorCS"),sQuery(id+"F8.wireOp",EDGE,"E87.79.MirrorCS"),sQuery(id+"F8.wireOp",EDGE,"E87.80.MirrorCS"),sQuery(id+"F8.wireOp",EDGE,"E87.81.MirrorCS"),sQuery(id+"F8.wireOp",EDGE,"E87.82.MirrorCS"),sQuery(id+"F8.wireOp",EDGE,"E87.83.MirrorCS"),sQuery(id+"F8.wireOp",EDGE,"E87.84.MirrorCS")])]}),"instanceName":"3"});
            var Q6;
            Q6=makeQuery(id+"F17.opPattern","COPY",BODY,{"derivedFrom":makeQuery(id+"F9.opExtrude","SWEPT_BODY",BODY,{"disambiguationData":[OSD([sQuery(id+"F8.wireOp",EDGE,"E82"),sQuery(id+"F8.wireOp",EDGE,"E83"),sQuery(id+"F8.wireOp",EDGE,"E84"),sQuery(id+"F8.wireOp",EDGE,"E85"),sQuery(id+"F8.wireOp",EDGE,"E86"),sQuery(id+"F8.wireOp",EDGE,"E87.13.MirrorCS"),sQuery(id+"F8.wireOp",EDGE,"E87.31.MirrorCS"),sQuery(id+"F8.wireOp",EDGE,"E87.33.MirrorCS"),sQuery(id+"F8.wireOp",EDGE,"E87.64.MirrorCS"),sQuery(id+"F8.wireOp",EDGE,"E87.22.MirrorCS")])]}),"instanceName":"3"});
            var Q7;
            Q7=makeQuery(id+"F17.opPattern","COPY",BODY,{"derivedFrom":makeQuery(id+"F9.opExtrude","SWEPT_BODY",BODY,{"disambiguationData":[OSD([sQuery(id+"F8.wireOp",EDGE,"E8"),sQuery(id+"F8.wireOp",EDGE,"E9"),sQuery(id+"F8.wireOp",EDGE,"E10"),sQuery(id+"F8.wireOp",EDGE,"E11"),sQuery(id+"F8.wireOp",EDGE,"E12.filletArc"),sQuery(id+"F8.wireOp",EDGE,"E13.filletArc"),sQuery(id+"F8.wireOp",EDGE,"E14.0"),sQuery(id+"F8.wireOp",EDGE,"E14.1"),sQuery(id+"F8.wireOp",EDGE,"E14.2"),sQuery(id+"F8.wireOp",EDGE,"E15"),sQuery(id+"F8.wireOp",EDGE,"E16"),sQuery(id+"F8.wireOp",EDGE,"E17"),sQuery(id+"F8.wireOp",EDGE,"E18"),sQuery(id+"F8.wireOp",EDGE,"E19.0"),sQuery(id+"F8.wireOp",EDGE,"E19.1"),sQuery(id+"F8.wireOp",EDGE,"E19.2"),sQuery(id+"F8.wireOp",EDGE,"E20"),sQuery(id+"F8.wireOp",EDGE,"E21.trimOffspring"),sQuery(id+"F8.wireOp",EDGE,"E22"),sQuery(id+"F8.wireOp",EDGE,"E23.trimOffspring"),sQuery(id+"F8.wireOp",EDGE,"E24.trimOffspring"),sQuery(id+"F8.wireOp",EDGE,"E25"),sQuery(id+"F8.wireOp",EDGE,"E26"),sQuery(id+"F8.wireOp",EDGE,"E27"),sQuery(id+"F8.wireOp",EDGE,"E28.trimOffspring"),sQuery(id+"F8.wireOp",EDGE,"E29"),sQuery(id+"F8.wireOp",EDGE,"E30"),sQuery(id+"F8.wireOp",EDGE,"E31"),sQuery(id+"F8.wireOp",EDGE,"E32"),sQuery(id+"F8.wireOp",EDGE,"E33"),sQuery(id+"F8.wireOp",EDGE,"E34"),sQuery(id+"F8.wireOp",EDGE,"E35.trimOffspring"),sQuery(id+"F8.wireOp",EDGE,"E36"),sQuery(id+"F8.wireOp",EDGE,"E37"),sQuery(id+"F8.wireOp",EDGE,"E38"),sQuery(id+"F8.wireOp",EDGE,"E39"),sQuery(id+"F8.wireOp",EDGE,"E40"),sQuery(id+"F8.wireOp",EDGE,"E41"),sQuery(id+"F8.wireOp",EDGE,"E42.trimOffspring"),sQuery(id+"F8.wireOp",EDGE,"E43"),sQuery(id+"F8.wireOp",EDGE,"E44"),sQuery(id+"F8.wireOp",EDGE,"E45"),sQuery(id+"F8.wireOp",EDGE,"E46.trimOffspring"),sQuery(id+"F8.wireOp",EDGE,"E47"),sQuery(id+"F8.wireOp",EDGE,"E48"),sQuery(id+"F8.wireOp",EDGE,"E49"),sQuery(id+"F8.wireOp",EDGE,"E50"),sQuery(id+"F8.wireOp",EDGE,"E51"),sQuery(id+"F8.wireOp",EDGE,"E52"),sQuery(id+"F8.wireOp",EDGE,"E53"),sQuery(id+"F8.wireOp",EDGE,"E54.trimOffspring"),sQuery(id+"F8.wireOp",EDGE,"E55.trimOffspring"),sQuery(id+"F8.wireOp",EDGE,"E56.trimOffspring"),sQuery(id+"F8.wireOp",EDGE,"E57.trimOffspring"),sQuery(id+"F8.wireOp",EDGE,"E58.trimOffspring"),sQuery(id+"F8.wireOp",EDGE,"E59"),sQuery(id+"F8.wireOp",EDGE,"E60"),sQuery(id+"F8.wireOp",EDGE,"E61"),sQuery(id+"F8.wireOp",EDGE,"E62"),sQuery(id+"F8.wireOp",EDGE,"E63.trimOffspring"),sQuery(id+"F8.wireOp",EDGE,"E64"),sQuery(id+"F8.wireOp",EDGE,"E65"),sQuery(id+"F8.wireOp",EDGE,"E66"),sQuery(id+"F8.wireOp",EDGE,"E67"),sQuery(id+"F8.wireOp",EDGE,"E68"),sQuery(id+"F8.wireOp",EDGE,"E69"),sQuery(id+"F8.wireOp",EDGE,"E70"),sQuery(id+"F8.wireOp",EDGE,"E71"),sQuery(id+"F8.wireOp",EDGE,"E72"),sQuery(id+"F8.wireOp",EDGE,"E73.trimOffspring"),sQuery(id+"F8.wireOp",EDGE,"E74.trimOffspring"),sQuery(id+"F8.wireOp",EDGE,"E75.trimOffspring"),sQuery(id+"F8.wireOp",EDGE,"E76.trimOffspring"),sQuery(id+"F8.wireOp",EDGE,"E77"),sQuery(id+"F8.wireOp",EDGE,"E78"),sQuery(id+"F8.wireOp",EDGE,"E79"),sQuery(id+"F8.wireOp",EDGE,"E80"),sQuery(id+"F8.wireOp",EDGE,"E81.trimOffspring"),sQuery(id+"F8.wireOp",EDGE,"E87.0.MirrorCS"),sQuery(id+"F8.wireOp",EDGE,"E87.1.MirrorCS"),sQuery(id+"F8.wireOp",EDGE,"E87.2.MirrorCS"),sQuery(id+"F8.wireOp",EDGE,"E87.3.MirrorCS"),sQuery(id+"F8.wireOp",EDGE,"E87.5.MirrorCS"),sQuery(id+"F8.wireOp",EDGE,"E87.6.MirrorCS"),sQuery(id+"F8.wireOp",EDGE,"E87.7.MirrorCS"),sQuery(id+"F8.wireOp",EDGE,"E87.8.MirrorCS"),sQuery(id+"F8.wireOp",EDGE,"E87.9.MirrorCS"),sQuery(id+"F8.wireOp",EDGE,"E87.10.MirrorCS"),sQuery(id+"F8.wireOp",EDGE,"E87.11.MirrorCS"),sQuery(id+"F8.wireOp",EDGE,"E87.12.MirrorCS"),sQuery(id+"F8.wireOp",EDGE,"E87.14.MirrorCS"),sQuery(id+"F8.wireOp",EDGE,"E87.15.MirrorCS"),sQuery(id+"F8.wireOp",EDGE,"E87.16.MirrorCS"),sQuery(id+"F8.wireOp",EDGE,"E87.17.MirrorCS"),sQuery(id+"F8.wireOp",EDGE,"E87.18.MirrorCS"),sQuery(id+"F8.wireOp",EDGE,"E87.19.MirrorCS"),sQuery(id+"F8.wireOp",EDGE,"E87.20.MirrorCS"),sQuery(id+"F8.wireOp",EDGE,"E87.21.MirrorCS"),sQuery(id+"F8.wireOp",EDGE,"E87.23.MirrorCS"),sQuery(id+"F8.wireOp",EDGE,"E87.24.MirrorCS"),sQuery(id+"F8.wireOp",EDGE,"E87.25.MirrorCS"),sQuery(id+"F8.wireOp",EDGE,"E87.26.MirrorCS"),sQuery(id+"F8.wireOp",EDGE,"E87.27.MirrorCS"),sQuery(id+"F8.wireOp",EDGE,"E87.28.MirrorCS"),sQuery(id+"F8.wireOp",EDGE,"E87.29.MirrorCS"),sQuery(id+"F8.wireOp",EDGE,"E87.30.MirrorCS"),sQuery(id+"F8.wireOp",EDGE,"E87.32.MirrorCS"),sQuery(id+"F8.wireOp",EDGE,"E87.34.MirrorCS"),sQuery(id+"F8.wireOp",EDGE,"E87.35.MirrorCS"),sQuery(id+"F8.wireOp",EDGE,"E87.36.MirrorCS"),sQuery(id+"F8.wireOp",EDGE,"E87.37.MirrorCS"),sQuery(id+"F8.wireOp",EDGE,"E87.38.MirrorCS"),sQuery(id+"F8.wireOp",EDGE,"E87.39.MirrorCS"),sQuery(id+"F8.wireOp",EDGE,"E87.40.MirrorCS"),sQuery(id+"F8.wireOp",EDGE,"E87.41.MirrorCS"),sQuery(id+"F8.wireOp",EDGE,"E87.42.MirrorCS"),sQuery(id+"F8.wireOp",EDGE,"E87.43.MirrorCS"),sQuery(id+"F8.wireOp",EDGE,"E87.44.MirrorCS"),sQuery(id+"F8.wireOp",EDGE,"E87.45.MirrorCS"),sQuery(id+"F8.wireOp",EDGE,"E87.46.MirrorCS"),sQuery(id+"F8.wireOp",EDGE,"E87.47.MirrorCS"),sQuery(id+"F8.wireOp",EDGE,"E87.48.MirrorCS"),sQuery(id+"F8.wireOp",EDGE,"E87.49.MirrorCS"),sQuery(id+"F8.wireOp",EDGE,"E87.50.MirrorCS"),sQuery(id+"F8.wireOp",EDGE,"E87.51.MirrorCS"),sQuery(id+"F8.wireOp",EDGE,"E87.53.MirrorCS"),sQuery(id+"F8.wireOp",EDGE,"E87.54.MirrorCS"),sQuery(id+"F8.wireOp",EDGE,"E87.55.MirrorCS"),sQuery(id+"F8.wireOp",EDGE,"E87.56.MirrorCS"),sQuery(id+"F8.wireOp",EDGE,"E87.57.MirrorCS"),sQuery(id+"F8.wireOp",EDGE,"E87.58.MirrorCS"),sQuery(id+"F8.wireOp",EDGE,"E87.59.MirrorCS"),sQuery(id+"F8.wireOp",EDGE,"E87.60.MirrorCS"),sQuery(id+"F8.wireOp",EDGE,"E87.61.MirrorCS"),sQuery(id+"F8.wireOp",EDGE,"E87.62.MirrorCS"),sQuery(id+"F8.wireOp",EDGE,"E87.63.MirrorCS"),sQuery(id+"F8.wireOp",EDGE,"E87.65.MirrorCS"),sQuery(id+"F8.wireOp",EDGE,"E87.66.MirrorCS"),sQuery(id+"F8.wireOp",EDGE,"E87.67.MirrorCS"),sQuery(id+"F8.wireOp",EDGE,"E87.68.MirrorCS"),sQuery(id+"F8.wireOp",EDGE,"E87.69.MirrorCS"),sQuery(id+"F8.wireOp",EDGE,"E87.70.MirrorCS"),sQuery(id+"F8.wireOp",EDGE,"E87.71.MirrorCS"),sQuery(id+"F8.wireOp",EDGE,"E87.72.MirrorCS"),sQuery(id+"F8.wireOp",EDGE,"E87.73.MirrorCS"),sQuery(id+"F8.wireOp",EDGE,"E87.74.MirrorCS"),sQuery(id+"F8.wireOp",EDGE,"E87.75.MirrorCS"),sQuery(id+"F8.wireOp",EDGE,"E87.76.MirrorCS"),sQuery(id+"F8.wireOp",EDGE,"E87.77.MirrorCS"),sQuery(id+"F8.wireOp",EDGE,"E87.78.MirrorCS"),sQuery(id+"F8.wireOp",EDGE,"E87.79.MirrorCS"),sQuery(id+"F8.wireOp",EDGE,"E87.80.MirrorCS"),sQuery(id+"F8.wireOp",EDGE,"E87.81.MirrorCS"),sQuery(id+"F8.wireOp",EDGE,"E87.82.MirrorCS"),sQuery(id+"F8.wireOp",EDGE,"E87.83.MirrorCS"),sQuery(id+"F8.wireOp",EDGE,"E87.84.MirrorCS")])]}),"instanceName":"2"});
            var Q8;
            Q8=makeQuery(id+"F17.opPattern","COPY",BODY,{"derivedFrom":makeQuery(id+"F9.opExtrude","SWEPT_BODY",BODY,{"disambiguationData":[OSD([sQuery(id+"F8.wireOp",EDGE,"E82"),sQuery(id+"F8.wireOp",EDGE,"E83"),sQuery(id+"F8.wireOp",EDGE,"E84"),sQuery(id+"F8.wireOp",EDGE,"E85"),sQuery(id+"F8.wireOp",EDGE,"E86"),sQuery(id+"F8.wireOp",EDGE,"E87.13.MirrorCS"),sQuery(id+"F8.wireOp",EDGE,"E87.31.MirrorCS"),sQuery(id+"F8.wireOp",EDGE,"E87.33.MirrorCS"),sQuery(id+"F8.wireOp",EDGE,"E87.64.MirrorCS"),sQuery(id+"F8.wireOp",EDGE,"E87.22.MirrorCS")])]}),"instanceName":"2"});
            var Q9;
            Q9=qCreatedBy(makeId("Right.planeOp"),FACE);
            mirror(context, id + "F29", {"entities" : qUnion([Q0, Q1, Q2, Q3, Q4, Q5, Q6, Q7, Q8]), "mirrorPlane" : qUnion([Q9])});
        }
    });
